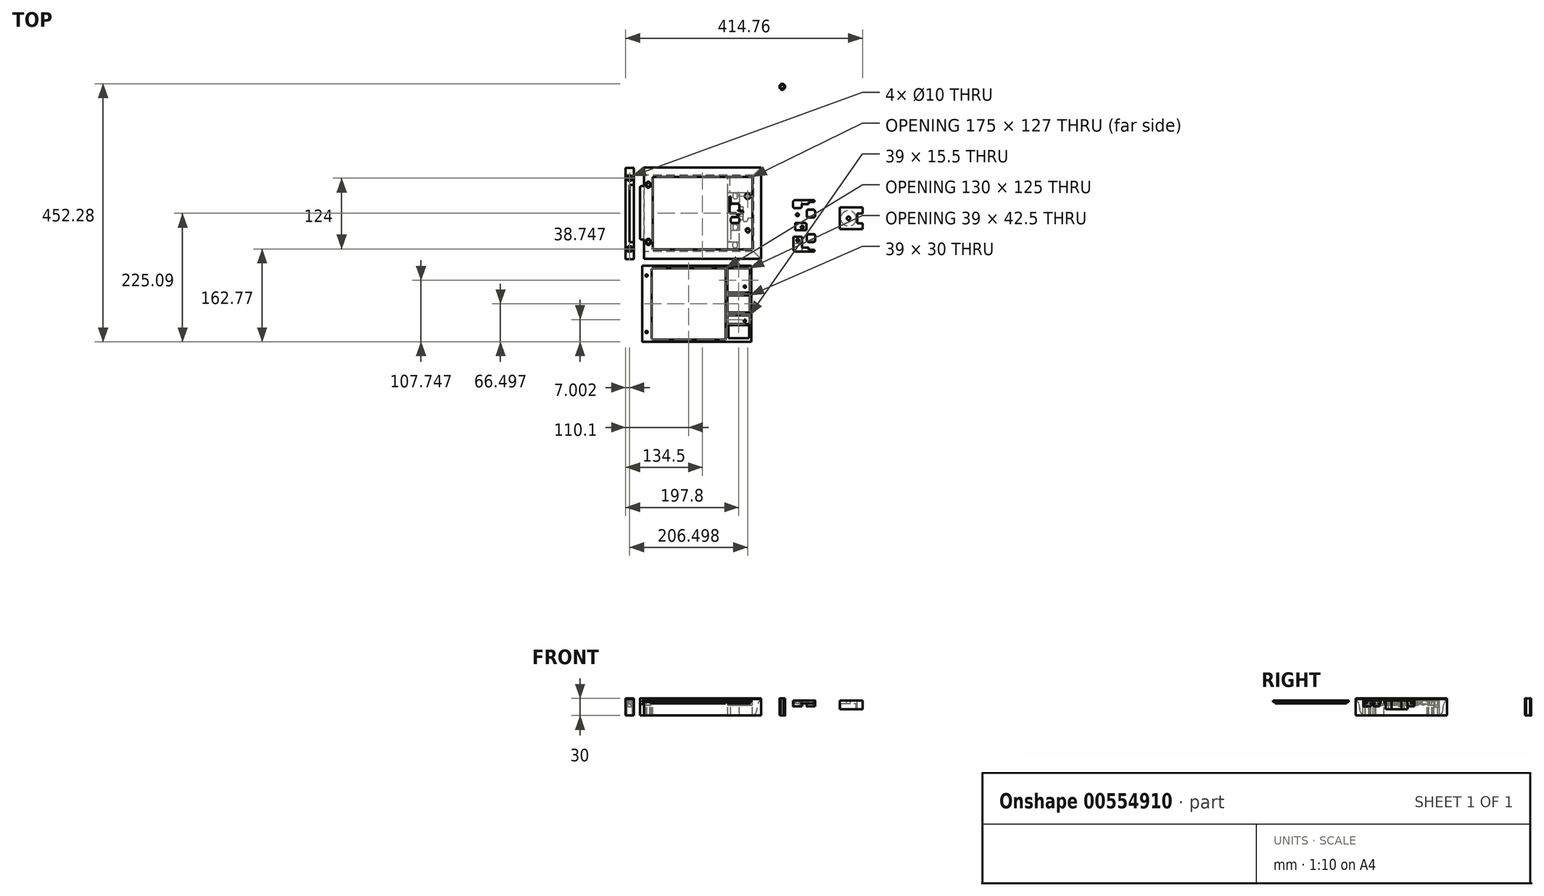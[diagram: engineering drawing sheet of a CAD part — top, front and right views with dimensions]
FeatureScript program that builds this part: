
annotation { "Feature Type Name" : "Feature", "Feature Type Description" : "" }
export const myFeature = defineFeature(function(context is Context, id is Id, definition is map)
    precondition{}
    {
        {
            var Q0;
            Q0=qCreatedBy(makeId("Top.planeOp"),FACE);
            var sketch = newSketch(context, id + "F0", { "sketchPlane" : qUnion([Q0])});
            skLineSegment(sketch, "E0.bottom", {"start": v(-107.5, 80) * mm, "end": v(97.5, 80) * mm});
            skLineSegment(sketch, "E0.top", {"start": v(-97.5, 0) * mm, "end": v(97.5, 0) * mm, "construction": true});
            skLineSegment(sketch, "E0.right", {"start": v(97.5, 80) * mm, "end": v(97.5, 0) * mm});
            skLineSegment(sketch, "E1.bottom", {"start": v(-92.5, 63.5) * mm, "end": v(82.5, 63.5) * mm});
            skLineSegment(sketch, "E1.left", {"start": v(-107.5, 63.5) * mm, "end": v(-107.5, -5) * mm});
            skLineSegment(sketch, "E1.right", {"start": v(82.5, 63.5) * mm, "end": v(82.5, 0) * mm});
            skLineSegment(sketch, "E2.right", {"start": v(42.5, 65) * mm, "end": v(42.5, 0) * mm});
            skLineSegment(sketch, "E3.MirrorCS", {"start": v(-92.5, -63.5) * mm, "end": v(82.5, -63.5) * mm});
            skLineSegment(sketch, "E4.MirrorCS", {"start": v(-107.5, -63.5) * mm, "end": v(-107.5, 5) * mm});
            skLineSegment(sketch, "E5.MirrorCS", {"start": v(-107.5, -80) * mm, "end": v(97.5, -80) * mm});
            skLineSegment(sketch, "E6.MirrorCS", {"start": v(97.5, -80) * mm, "end": v(97.5, 0) * mm});
            skLineSegment(sketch, "E7.MirrorCS", {"start": v(47.5, -4.97) * mm, "end": v(56.5, -4.97) * mm});
            skLineSegment(sketch, "E8.MirrorCS", {"start": v(44.5, -13.97) * mm, "end": v(44.5, -9.97) * mm});
            skLineSegment(sketch, "E9.MirrorCS", {"start": v(82.5, -63.5) * mm, "end": v(82.5, 0) * mm});
            skLineSegment(sketch, "E10.MirrorCS", {"start": v(59.5, -13.97) * mm, "end": v(59.5, -9.97) * mm});
            skLineSegment(sketch, "E11.MirrorCS", {"start": v(42.5, -63.5) * mm, "end": v(42.5, 0) * mm});
            skLineSegment(sketch, "E12", {"start": v(-107.5, -63.5) * mm, "end": v(-107.5, -80) * mm});
            skLineSegment(sketch, "E13", {"start": v(-107.5, 63.5) * mm, "end": v(-107.5, 80) * mm});
            skLineSegment(sketch, "E14.left", {"start": v(-132.5, 79.68) * mm, "end": v(-132.5, -0.32) * mm});
            skLineSegment(sketch, "E15.MirrorCS", {"start": v(-132.5, -80.32) * mm, "end": v(-132.5, -10.32) * mm});
            skPoint(sketch, "E16", {"position": v(-132.5, -50.32) * mm});
            skLineSegment(sketch, "E17", {"start": v(-132.5, -50.32) * mm, "end": v(-127.5, -50.32) * mm});
            skPoint(sketch, "E18", {"position": v(-132.5, 49.68) * mm});
            skLineSegment(sketch, "E19", {"start": v(-132.5, 49.68) * mm, "end": v(-127.5, 49.68) * mm});
            skLineSegment(sketch, "E20", {"start": v(-114.5, -30.14) * mm, "end": v(-114.5, 44.86) * mm});
            skLineSegment(sketch, "E21", {"start": v(-127.5, -50.32) * mm, "end": v(-125.5, -50.32) * mm});
            skLineSegment(sketch, "E22", {"start": v(-125.5, -50.32) * mm, "end": v(-125.5, -80.32) * mm});
            skLineSegment(sketch, "E23", {"start": v(-125.5, -50.32) * mm, "end": v(-125.5, 79.68) * mm});
            skLineSegment(sketch, "E24", {"start": v(-127.5, 49.68) * mm, "end": v(-125.5, 49.68) * mm});
            skLineSegment(sketch, "E25", {"start": v(-107.5, -80) * mm, "end": v(-92.5, -80) * mm});
            skLineSegment(sketch, "E26", {"start": v(-92.5, -80) * mm, "end": v(-92.5, 63.5) * mm});
            skLineSegment(sketch, "E27", {"start": v(47.5, -16.97) * mm, "end": v(56.5, -16.97) * mm});
            skLineSegment(sketch, "E28", {"start": v(47.5, -6.97) * mm, "end": v(56.5, -6.97) * mm});
            skLineSegment(sketch, "E29", {"start": v(47.5, -18.97) * mm, "end": v(56.5, -18.97) * mm});
            skLineSegment(sketch, "E30", {"start": v(46.02, -30.47) * mm, "end": v(53.02, -30.47) * mm});
            skLineSegment(sketch, "E31", {"start": v(44.5, -63.15) * mm, "end": v(56.5, -63.15) * mm});
            skLineSegment(sketch, "E32", {"start": v(59.5, -58.47) * mm, "end": v(59.5, -51.47) * mm});
            skArc(sketch, "E33.filletArc", {"start": v(47.5, -4.97) * mm, "mid": v(45.38, -5.85) * mm, "end": v(44.5, -7.97) * mm});
            skLineSegment(sketch, "E34", {"start": v(44.5, -45) * mm, "end": v(44.5, -27.47) * mm});
            skLineSegment(sketch, "E35", {"start": v(59.5, -27.47) * mm, "end": v(59.5, -45) * mm});
            skCircle(sketch, "E36", {"center": v(52, -55.5) * mm, "radius": 2.55 * mm});
            skCircle(sketch, "E37.MirrorC", {"center": v(52, 30.47) * mm, "radius": 2.55 * mm});
            skLineSegment(sketch, "E38.MirrorCS", {"start": v(44.5, 36.5) * mm, "end": v(44.5, 27.47) * mm});
            skLineSegment(sketch, "E39.MirrorCS", {"start": v(59.5, 27.47) * mm, "end": v(59.5, 33.5) * mm});
            skLineSegment(sketch, "E40", {"start": v(44.5, -49.9) * mm, "end": v(57.5, -49.9) * mm});
            skLineSegment(sketch, "E41", {"start": v(-132.5, 79.68) * mm, "end": v(-125.5, 79.68) * mm});
            skLineSegment(sketch, "E42", {"start": v(-132.5, -80.32) * mm, "end": v(-125.5, -80.32) * mm});
            skLineSegment(sketch, "E43", {"start": v(39.5, 36.5) * mm, "end": v(44.5, 36.5) * mm});
            skLineSegment(sketch, "E44", {"start": v(39.5, 29.5) * mm, "end": v(44.5, 29.5) * mm});
            skLineSegment(sketch, "E45", {"start": v(82.5, 0) * mm, "end": v(42.5, 0) * mm});
            skCircle(sketch, "E46", {"center": v(57.5, 0) * mm, "radius": 3 * mm});
            skLineSegment(sketch, "E47", {"start": v(47.9, 28.33) * mm, "end": v(47.9, 32.6) * mm});
            skLineSegment(sketch, "E48", {"start": v(56.1, 28.33) * mm, "end": v(56.1, 32.6) * mm});
            skLineSegment(sketch, "E49", {"start": v(50.28, 25.92) * mm, "end": v(47.9, 27.58) * mm});
            skLineSegment(sketch, "E50", {"start": v(53.72, 25.92) * mm, "end": v(56.1, 27.58) * mm});
            skLineSegment(sketch, "E51", {"start": v(53.72, 35.02) * mm, "end": v(56.1, 33.36) * mm});
            skLineSegment(sketch, "E52", {"start": v(50.28, 35.02) * mm, "end": v(47.9, 33.36) * mm});
            skLineSegment(sketch, "E53", {"start": v(47.9, -57.64) * mm, "end": v(47.9, -53.37) * mm});
            skLineSegment(sketch, "E54", {"start": v(56.1, -57.64) * mm, "end": v(56.1, -53.37) * mm});
            skLineSegment(sketch, "E55", {"start": v(50.28, -60.05) * mm, "end": v(47.9, -58.4) * mm});
            skLineSegment(sketch, "E56", {"start": v(53.72, -60.05) * mm, "end": v(56.1, -58.4) * mm});
            skLineSegment(sketch, "E57", {"start": v(53.72, -50.94) * mm, "end": v(56.1, -52.6) * mm});
            skLineSegment(sketch, "E58", {"start": v(50.28, -50.94) * mm, "end": v(47.9, -52.6) * mm});
            skCircle(sketch, "E59.MirrorC", {"center": v(52, -24.47) * mm, "radius": 2.55 * mm});
            skLineSegment(sketch, "E60", {"start": v(47.9, -26.61) * mm, "end": v(47.9, -22.33) * mm});
            skLineSegment(sketch, "E61", {"start": v(56.1, -26.61) * mm, "end": v(56.1, -22.33) * mm});
            skLineSegment(sketch, "E62", {"start": v(50.28, -29.02) * mm, "end": v(47.9, -27.36) * mm});
            skLineSegment(sketch, "E63", {"start": v(53.72, -29.02) * mm, "end": v(56.1, -27.36) * mm});
            skLineSegment(sketch, "E64", {"start": v(53.72, -19.92) * mm, "end": v(56.1, -21.58) * mm});
            skLineSegment(sketch, "E65", {"start": v(50.28, -19.92) * mm, "end": v(47.9, -21.58) * mm});
            skArc(sketch, "E66.filletArc", {"start": v(44.5, -13.97) * mm, "mid": v(45.38, -16.1) * mm, "end": v(47.5, -16.97) * mm});
            skArc(sketch, "E67.filletArc", {"start": v(56.5, -16.97) * mm, "mid": v(58.62, -16.1) * mm, "end": v(59.5, -13.97) * mm});
            skLineSegment(sketch, "E68", {"start": v(44.5, -13.97) * mm, "end": v(44.5, -15.97) * mm});
            skLineSegment(sketch, "E69", {"start": v(59.5, -13.97) * mm, "end": v(59.5, -15.97) * mm});
            skArc(sketch, "E70.filletArc", {"start": v(44.5, -15.97) * mm, "mid": v(45.38, -18.1) * mm, "end": v(47.5, -18.97) * mm});
            skArc(sketch, "E71.filletArc", {"start": v(56.5, -18.97) * mm, "mid": v(58.62, -18.1) * mm, "end": v(59.5, -15.97) * mm});
            skLineSegment(sketch, "E72", {"start": v(44.5, -15.97) * mm, "end": v(44.5, -25.97) * mm});
            skLineSegment(sketch, "E73", {"start": v(59.5, -25.97) * mm, "end": v(59.5, -15.97) * mm});
            skArc(sketch, "E74.filletArc", {"start": v(47.5, -6.97) * mm, "mid": v(45.38, -7.85) * mm, "end": v(44.5, -9.97) * mm});
            skArc(sketch, "E75.filletArc", {"start": v(59.5, -9.97) * mm, "mid": v(58.62, -7.85) * mm, "end": v(56.5, -6.97) * mm});
            skLineSegment(sketch, "E76", {"start": v(44.5, -9.97) * mm, "end": v(44.5, -7.97) * mm});
            skLineSegment(sketch, "E77", {"start": v(44.5, 13.97) * mm, "end": v(44.5, 13.97) * mm});
            skLineSegment(sketch, "E78", {"start": v(59.5, 27.47) * mm, "end": v(59.5, 15.97) * mm});
            skLineSegment(sketch, "E79", {"start": v(59.5, -45) * mm, "end": v(59.5, -51.47) * mm});
            skLineSegment(sketch, "E80", {"start": v(59.5, -58.47) * mm, "end": v(59.5, -60.15) * mm});
            skArc(sketch, "E81.filletArc", {"start": v(56.5, -63.15) * mm, "mid": v(58.62, -62.27) * mm, "end": v(59.5, -60.15) * mm});
            skLineSegment(sketch, "E82", {"start": v(-132.5, -10.32) * mm, "end": v(-132.5, -0.32) * mm});
            skLineSegment(sketch, "E83", {"start": v(-132.5, -50.32) * mm, "end": v(-139.5, -50.32) * mm});
            skLineSegment(sketch, "E84", {"start": v(-132.5, 49.68) * mm, "end": v(-139.5, 49.68) * mm});
            skLineSegment(sketch, "E85", {"start": v(39.5, -63.5) * mm, "end": v(39.5, 63.5) * mm});
            skLineSegment(sketch, "E86", {"start": v(46.02, -30.47) * mm, "end": v(44.5, -30.47) * mm});
            skLineSegment(sketch, "E87", {"start": v(53.02, -30.47) * mm, "end": v(59.5, -30.47) * mm});
            skLineSegment(sketch, "E88", {"start": v(42.5, 29.5) * mm, "end": v(39.5, 29.5) * mm});
            skLineSegment(sketch, "E89", {"start": v(42.5, 36.5) * mm, "end": v(39.5, 36.5) * mm});
            skLineSegment(sketch, "E90", {"start": v(43.5, -49.9) * mm, "end": v(40.5, -49.9) * mm});
            skLineSegment(sketch, "E91", {"start": v(55.5, -49.9) * mm, "end": v(45.5, -49.9) * mm});
            skLineSegment(sketch, "E92", {"start": v(44.5, -30.47) * mm, "end": v(59.5, -30.47) * mm});
            skLineSegment(sketch, "E93", {"start": v(59.5, -30.47) * mm, "end": v(59.5, -50) * mm});
            skLineSegment(sketch, "E94", {"start": v(-111.5, 47.86) * mm, "end": v(-107.5, 47.86) * mm});
            skLineSegment(sketch, "E95", {"start": v(-114.5, -30.14) * mm, "end": v(-114.5, -43.14) * mm});
            skLineSegment(sketch, "E96", {"start": v(-111.5, -46.14) * mm, "end": v(-107.5, -46.14) * mm});
            skPoint(sketch, "E97.end.orphan", {"position": v(-107.5, 59.86) * mm});
            skLineSegment(sketch, "E98", {"start": v(40.5, -49.9) * mm, "end": v(39.5, -49.9) * mm});
            skPoint(sketch, "E99", {"position": v(-100, -50) * mm});
            skLineSegment(sketch, "E100", {"start": v(-103.5, -52.14) * mm, "end": v(-103.5, -47.87) * mm});
            skLineSegment(sketch, "E101", {"start": v(-96.5, -52.14) * mm, "end": v(-96.5, -47.87) * mm});
            skLineSegment(sketch, "E102", {"start": v(-101.72, -54.89) * mm, "end": v(-103.5, -53.64) * mm});
            skLineSegment(sketch, "E103", {"start": v(-98.28, -45.12) * mm, "end": v(-96.5, -46.37) * mm});
            skLineSegment(sketch, "E104", {"start": v(-101.72, -45.12) * mm, "end": v(-103.5, -46.37) * mm});
            skLineSegment(sketch, "E105", {"start": v(-96.5, -53.64) * mm, "end": v(-98.28, -54.89) * mm});
            skLineSegment(sketch, "E106", {"start": v(44.5, -45) * mm, "end": v(44.5, -63.5) * mm});
            skLineSegment(sketch, "E107", {"start": v(59.5, -25.97) * mm, "end": v(59.5, -27.47) * mm});
            skLineSegment(sketch, "E108", {"start": v(44.5, -25.97) * mm, "end": v(44.5, -27.47) * mm});
            skArc(sketch, "E109.filletArc", {"start": v(-114.5, -43.14) * mm, "mid": v(-113.62, -45.26) * mm, "end": v(-111.5, -46.14) * mm});
            skArc(sketch, "E110.filletArc", {"start": v(-111.5, 47.86) * mm, "mid": v(-113.62, 46.98) * mm, "end": v(-114.5, 44.86) * mm});
            skLineSegment(sketch, "E111.MirrorCS", {"start": v(-103.5, 52.14) * mm, "end": v(-103.5, 47.87) * mm});
            skLineSegment(sketch, "E112.MirrorCS", {"start": v(-101.72, 45.12) * mm, "end": v(-103.5, 46.37) * mm});
            skLineSegment(sketch, "E113.MirrorCS", {"start": v(-96.5, 52.14) * mm, "end": v(-96.5, 47.87) * mm});
            skPoint(sketch, "E114.MirrorP", {"position": v(-100, 50) * mm});
            skLineSegment(sketch, "E115.MirrorCS", {"start": v(-96.5, 53.64) * mm, "end": v(-98.28, 54.89) * mm});
            skLineSegment(sketch, "E116.MirrorCS", {"start": v(-98.28, 45.12) * mm, "end": v(-96.5, 46.37) * mm});
            skLineSegment(sketch, "E117.MirrorCS", {"start": v(-101.72, 54.89) * mm, "end": v(-103.5, 53.64) * mm});
            skLineSegment(sketch, "E118", {"start": v(57.5, -63.15) * mm, "end": v(42.5, -63.15) * mm});
            skLineSegment(sketch, "E119", {"start": v(42.5, -63.15) * mm, "end": v(39.5, -63.15) * mm});
            skArc(sketch, "E120.filletArc", {"start": v(53.72, -50.94) * mm, "mid": v(52, -50.4) * mm, "end": v(50.28, -50.94) * mm});
            skArc(sketch, "E121.filletArc", {"start": v(50.28, -60.05) * mm, "mid": v(52, -60.6) * mm, "end": v(53.72, -60.05) * mm});
            skLineSegment(sketch, "E122", {"start": v(47.9, -52.6) * mm, "end": v(47.9, -53.37) * mm});
            skLineSegment(sketch, "E123", {"start": v(56.1, -52.6) * mm, "end": v(56.1, -53.37) * mm});
            skLineSegment(sketch, "E124", {"start": v(47.9, -58.4) * mm, "end": v(47.9, -57.64) * mm});
            skLineSegment(sketch, "E125", {"start": v(56.1, -58.4) * mm, "end": v(56.1, -57.64) * mm});
            skArc(sketch, "E126.filletArc", {"start": v(53.72, -19.92) * mm, "mid": v(52, -19.38) * mm, "end": v(50.28, -19.92) * mm});
            skArc(sketch, "E127.filletArc", {"start": v(50.28, -29.02) * mm, "mid": v(52, -29.56) * mm, "end": v(53.72, -29.02) * mm});
            skLineSegment(sketch, "E128", {"start": v(47.9, -21.58) * mm, "end": v(47.9, -22.33) * mm});
            skLineSegment(sketch, "E129", {"start": v(56.1, -21.58) * mm, "end": v(56.1, -22.33) * mm});
            skLineSegment(sketch, "E130", {"start": v(47.9, -26.61) * mm, "end": v(47.9, -27.36) * mm});
            skLineSegment(sketch, "E131", {"start": v(56.1, -26.61) * mm, "end": v(56.1, -27.36) * mm});
            skArc(sketch, "E132.filletArc", {"start": v(53.72, 35.02) * mm, "mid": v(52, 35.56) * mm, "end": v(50.28, 35.02) * mm});
            skArc(sketch, "E133.filletArc", {"start": v(50.28, 25.92) * mm, "mid": v(52, 25.38) * mm, "end": v(53.72, 25.92) * mm});
            skLineSegment(sketch, "E134", {"start": v(47.9, 28.33) * mm, "end": v(47.9, 27.58) * mm});
            skLineSegment(sketch, "E135", {"start": v(56.1, 28.33) * mm, "end": v(56.1, 27.58) * mm});
            skLineSegment(sketch, "E136", {"start": v(47.9, 33.36) * mm, "end": v(47.9, 32.6) * mm});
            skLineSegment(sketch, "E137", {"start": v(56.1, 33.36) * mm, "end": v(56.1, 32.6) * mm});
            skArc(sketch, "E138.filletArc", {"start": v(-98.28, 54.89) * mm, "mid": v(-100, 55.43) * mm, "end": v(-101.72, 54.89) * mm});
            skArc(sketch, "E139.filletArc", {"start": v(-101.72, 45.12) * mm, "mid": v(-100, 44.58) * mm, "end": v(-98.28, 45.12) * mm});
            skArc(sketch, "E140.filletArc", {"start": v(-101.72, -54.89) * mm, "mid": v(-100, -55.43) * mm, "end": v(-98.28, -54.89) * mm});
            skArc(sketch, "E141.filletArc", {"start": v(-98.28, -45.12) * mm, "mid": v(-100, -44.58) * mm, "end": v(-101.72, -45.12) * mm});
            skLineSegment(sketch, "E142", {"start": v(57.5, -49.9) * mm, "end": v(59.5, -49.9) * mm});
            skLineSegment(sketch, "E143", {"start": v(39.5, -49.9) * mm, "end": v(44.5, -49.9) * mm});
            skLineSegment(sketch, "E144", {"start": v(-103.5, 46.37) * mm, "end": v(-103.5, 47.87) * mm});
            skLineSegment(sketch, "E145", {"start": v(-103.5, 52.14) * mm, "end": v(-103.5, 53.64) * mm});
            skLineSegment(sketch, "E146", {"start": v(-96.49, 52.16) * mm, "end": v(-96.5, 53.64) * mm});
            skLineSegment(sketch, "E147", {"start": v(-96.5, 46.37) * mm, "end": v(-96.5, 47.87) * mm});
            skLineSegment(sketch, "E148", {"start": v(-103.5, -53.64) * mm, "end": v(-103.5, -52.14) * mm});
            skLineSegment(sketch, "E149", {"start": v(-103.53, -47.9) * mm, "end": v(-103.5, -46.37) * mm});
            skLineSegment(sketch, "E150", {"start": v(-96.5, -47.87) * mm, "end": v(-96.5, -46.37) * mm});
            skLineSegment(sketch, "E151", {"start": v(-96.5, -53.64) * mm, "end": v(-96.5, -52.14) * mm});
            skCircle(sketch, "E152", {"center": v(-132.5, -62.32) * mm, "radius": 3.1 * mm});
            skCircle(sketch, "E153", {"center": v(-132.5, -62.32) * mm, "radius": 5 * mm});
            skLineSegment(sketch, "E154", {"start": v(-132.5, -0.32) * mm, "end": v(-139.5, -0.32) * mm});
            skCircle(sketch, "E155.MirrorC", {"center": v(-132.5, 61.68) * mm, "radius": 5 * mm});
            skCircle(sketch, "E156.MirrorC", {"center": v(-132.5, 61.68) * mm, "radius": 3.1 * mm});
            skLineSegment(sketch, "E157", {"start": v(-132.5, 79.68) * mm, "end": v(-139.5, 79.68) * mm});
            skLineSegment(sketch, "E158", {"start": v(-139.5, 79.68) * mm, "end": v(-139.5, -80.32) * mm});
            skLineSegment(sketch, "E159", {"start": v(-139.5, -80.32) * mm, "end": v(-132.5, -80.32) * mm});
            skCircle(sketch, "E160", {"center": v(-100, -50) * mm, "radius": 3.15 * mm});
            skCircle(sketch, "E161", {"center": v(-100, -50) * mm, "radius": 5 * mm});
            skCircle(sketch, "E162", {"center": v(-100, 50) * mm, "radius": 3.15 * mm});
            skCircle(sketch, "E163", {"center": v(-100, 50) * mm, "radius": 4.74 * mm});
            skLineSegment(sketch, "E164", {"start": v(44.5, 36.5) * mm, "end": v(56.5, 36.5) * mm});
            skArc(sketch, "E165.filletArc", {"start": v(59.5, 33.5) * mm, "mid": v(58.62, 35.62) * mm, "end": v(56.5, 36.5) * mm});
            skLineSegment(sketch, "E166", {"start": v(56.5, 36.5) * mm, "end": v(82.5, 36.5) * mm});
            skLineSegment(sketch, "E167", {"start": v(82.5, -8.5) * mm, "end": v(73.96, -8.5) * mm});
            skLineSegment(sketch, "E168", {"start": v(73.96, 8.5) * mm, "end": v(82.5, 8.5) * mm});
            skLineSegment(sketch, "E169", {"start": v(59.5, 11.47) * mm, "end": v(71.5, 11.48) * mm});
            skLineSegment(sketch, "E170", {"start": v(71.5, 11.48) * mm, "end": v(71.5, 4.98) * mm});
            skLineSegment(sketch, "E171", {"start": v(73.96, 8.5) * mm, "end": v(73.96, 11.5) * mm});
            skLineSegment(sketch, "E172", {"start": v(70.96, 14.5) * mm, "end": v(68.96, 14.5) * mm});
            skLineSegment(sketch, "E173", {"start": v(65.96, 11.5) * mm, "end": v(65.96, 0) * mm});
            skLineSegment(sketch, "E174.MirrorCS", {"start": v(71.5, -11.48) * mm, "end": v(71.5, -4.98) * mm});
            skLineSegment(sketch, "E175.MirrorCS", {"start": v(70.96, -14.5) * mm, "end": v(68.96, -14.5) * mm});
            skLineSegment(sketch, "E176.MirrorCS", {"start": v(73.96, -8.5) * mm, "end": v(73.96, -11.5) * mm});
            skLineSegment(sketch, "E177.MirrorCS", {"start": v(56.5, -4.97) * mm, "end": v(56.5, -4.97) * mm});
            skLineSegment(sketch, "E178.MirrorCS", {"start": v(59.5, -11.47) * mm, "end": v(71.5, -11.48) * mm});
            skLineSegment(sketch, "E179.MirrorCS", {"start": v(65.96, -11.5) * mm, "end": v(65.96, 0) * mm});
            skArc(sketch, "E180.filletArc", {"start": v(73.96, 11.5) * mm, "mid": v(73.08, 13.62) * mm, "end": v(70.96, 14.5) * mm});
            skArc(sketch, "E181.filletArc", {"start": v(68.96, 14.5) * mm, "mid": v(66.84, 13.62) * mm, "end": v(65.96, 11.5) * mm});
            skArc(sketch, "E182.filletArc", {"start": v(70.96, -14.5) * mm, "mid": v(73.08, -13.62) * mm, "end": v(73.96, -11.5) * mm});
            skArc(sketch, "E183.filletArc", {"start": v(65.96, -11.5) * mm, "mid": v(66.84, -13.62) * mm, "end": v(68.96, -14.5) * mm});
            skLineSegment(sketch, "E184", {"start": v(59.5, -9.97) * mm, "end": v(59.5, -7.97) * mm});
            skPoint(sketch, "E185.newPointA", {"position": v(71.5, 4.98) * mm});
            skLineSegment(sketch, "E186", {"start": v(56.5, 4.97) * mm, "end": v(71.5, 4.98) * mm});
            skPoint(sketch, "E187.newPointB", {"position": v(71.5, -4.98) * mm});
            skArc(sketch, "E187.filletArc", {"start": v(59.5, -7.97) * mm, "mid": v(58.62, -5.85) * mm, "end": v(56.5, -4.97) * mm});
            skLineSegment(sketch, "E188", {"start": v(56.5, -4.97) * mm, "end": v(71.5, -4.98) * mm});
            skLineSegment(sketch, "E189", {"start": v(44.5, 15.97) * mm, "end": v(44.5, 27.47) * mm});
            skLineSegment(sketch, "E190.MirrorCS", {"start": v(56.5, 4.97) * mm, "end": v(56.5, 4.97) * mm});
            skLineSegment(sketch, "E191.MirrorCS", {"start": v(59.5, 13.97) * mm, "end": v(59.5, 15.97) * mm});
            skLineSegment(sketch, "E192.MirrorCS", {"start": v(44.5, 9.97) * mm, "end": v(44.5, 7.97) * mm});
            skLineSegment(sketch, "E193.MirrorCS", {"start": v(47.5, 18.97) * mm, "end": v(56.5, 18.97) * mm});
            skLineSegment(sketch, "E194.MirrorCS", {"start": v(47.5, 6.97) * mm, "end": v(56.5, 6.97) * mm});
            skLineSegment(sketch, "E195.MirrorCS", {"start": v(47.5, 4.97) * mm, "end": v(56.5, 4.97) * mm});
            skArc(sketch, "E196.MirrorCS", {"start": v(47.5, 6.97) * mm, "mid": v(45.38, 7.85) * mm, "end": v(44.5, 9.97) * mm});
            skArc(sketch, "E197.MirrorCS", {"start": v(56.5, 16.97) * mm, "mid": v(58.62, 16.1) * mm, "end": v(59.5, 13.97) * mm});
            skLineSegment(sketch, "E198.MirrorCS", {"start": v(44.5, 13.97) * mm, "end": v(44.5, 15.97) * mm});
            skLineSegment(sketch, "E199.MirrorCS", {"start": v(59.5, 9.97) * mm, "end": v(59.5, 7.97) * mm});
            skArc(sketch, "E200.MirrorCS", {"start": v(47.5, 4.97) * mm, "mid": v(45.38, 5.85) * mm, "end": v(44.5, 7.97) * mm});
            skArc(sketch, "E201.MirrorCS", {"start": v(44.5, 13.97) * mm, "mid": v(45.38, 16.1) * mm, "end": v(47.5, 16.97) * mm});
            skArc(sketch, "E202.MirrorCS", {"start": v(44.5, 15.97) * mm, "mid": v(45.38, 18.1) * mm, "end": v(47.5, 18.97) * mm});
            skLineSegment(sketch, "E203.MirrorCS", {"start": v(44.5, 13.97) * mm, "end": v(44.5, 9.97) * mm});
            skLineSegment(sketch, "E204.MirrorCS", {"start": v(47.5, 16.97) * mm, "end": v(56.5, 16.97) * mm});
            skLineSegment(sketch, "E205.MirrorCS", {"start": v(59.5, 13.97) * mm, "end": v(59.5, 9.97) * mm});
            skArc(sketch, "E206.MirrorCS", {"start": v(59.5, 7.97) * mm, "mid": v(58.62, 5.85) * mm, "end": v(56.5, 4.97) * mm});
            skArc(sketch, "E207.MirrorCS", {"start": v(56.5, 18.97) * mm, "mid": v(58.62, 18.1) * mm, "end": v(59.5, 15.97) * mm});
            skArc(sketch, "E208.MirrorCS", {"start": v(59.5, 9.97) * mm, "mid": v(58.62, 7.85) * mm, "end": v(56.5, 6.97) * mm});
            skLineSegment(sketch, "E209.MirrorCS", {"start": v(131.25, 223.9) * mm, "end": v(131.25, 225.4) * mm});
            skLineSegment(sketch, "E210.MirrorCS", {"start": v(138.25, 223.9) * mm, "end": v(138.25, 219.63) * mm});
            skLineSegment(sketch, "E211.MirrorCS", {"start": v(138.25, 225.4) * mm, "end": v(136.47, 226.65) * mm});
            skLineSegment(sketch, "E212.MirrorCS", {"start": v(131.25, 219.63) * mm, "end": v(131.25, 218.13) * mm});
            skArc(sketch, "E213.MirrorCS", {"start": v(133.03, 226.65) * mm, "mid": v(134.75, 227.19) * mm, "end": v(136.47, 226.65) * mm});
            skLineSegment(sketch, "E214.MirrorCS", {"start": v(138.25, 219.63) * mm, "end": v(138.25, 218.13) * mm});
            skLineSegment(sketch, "E215.MirrorCS", {"start": v(131.25, 223.9) * mm, "end": v(131.25, 219.63) * mm});
            skLineSegment(sketch, "E216.MirrorCS", {"start": v(133.03, 226.65) * mm, "end": v(131.25, 225.4) * mm});
            skLineSegment(sketch, "E217.MirrorCS", {"start": v(136.47, 216.88) * mm, "end": v(138.25, 218.13) * mm});
            skLineSegment(sketch, "E218.MirrorCS", {"start": v(133.03, 216.88) * mm, "end": v(131.25, 218.13) * mm});
            skArc(sketch, "E219.MirrorCS", {"start": v(136.47, 216.88) * mm, "mid": v(134.75, 216.34) * mm, "end": v(133.03, 216.88) * mm});
            skPoint(sketch, "E220.MirrorP", {"position": v(134.75, 221.76) * mm});
            skLineSegment(sketch, "E221.MirrorCS", {"start": v(138.25, 223.9) * mm, "end": v(138.25, 225.4) * mm});
            skCircle(sketch, "E222", {"center": v(134.75, 221.76) * mm, "radius": 5 * mm});
            skCircle(sketch, "E223", {"center": v(134.75, 221.76) * mm, "radius": 3.15 * mm});
            skCircle(sketch, "E224", {"center": v(74, -30) * mm, "radius": 3.15 * mm});
            skCircle(sketch, "E225", {"center": v(74, -30) * mm, "radius": 5 * mm});
            skCircle(sketch, "E226.MirrorC", {"center": v(74, 30) * mm, "radius": 5 * mm});
            skCircle(sketch, "E227.MirrorC", {"center": v(74, 30) * mm, "radius": 3.15 * mm});
            skSolve(sketch);
        }
        {
            var Q0;
            {var subQ6=sQuery(id+"F0.wireOp",EDGE,"RdLYVHK0-ZMMy-n2T9-vo5N-ViF6aoFnglOa");Q0=makeQuery(id+"F0.imprint","IMPRINT",FACE,{"disambiguationData":[TD([[makeQuery(id+"F0.imprint","IMPRINT",EDGE,{"derivedFrom":subQ6}),-1.0]])]});}
            var Q1;
            {var subQ6=sQuery(id+"F0.wireOp",EDGE,"E40");Q1=makeQuery(id+"F0.imprint","IMPRINT",FACE,{"disambiguationData":[TD([[makeQuery(id+"F0.imprint","IMPRINT",EDGE,{"derivedFrom":subQ6}),-1.0]])]});}
            var Q2;
            {var subQ8=sQuery(id+"F0.wireOp",EDGE,"E39.MirrorCS");Q2=makeQuery(id+"F0.imprint","IMPRINT",FACE,{"disambiguationData":[TD([[makeQuery(id+"F0.imprint","IMPRINT",EDGE,{"derivedFrom":subQ8}),1.0]])]});}
            var Q3;
            Q3=makeQuery(id+"F0.imprint","IMPRINT",FACE,{"disambiguationData":[TD([[makeQuery(id+"F0.imprint","IMPRINT",EDGE,{"derivedFrom":sQuery(id+"F0.wireOp",EDGE,"E30")}),-1.0]])]});
            var Q4;
            {var subQ8=sQuery(id+"F0.wireOp",EDGE,"12c242b3-208e-4177-b4b7-cfe86d31bad3.filletArc");Q4=makeQuery(id+"F0.imprint","IMPRINT",FACE,{"disambiguationData":[TD([[makeQuery(id+"F0.imprint","IMPRINT",EDGE,{"derivedFrom":subQ8}),1.0]])]});}
            var Q5;
            {var subQ5=sQuery(id+"F0.wireOp",EDGE,"E31");Q5=makeQuery(id+"F0.imprint","IMPRINT",FACE,{"disambiguationData":[TD([[makeQuery(id+"F0.imprint","IMPRINT",EDGE,{"derivedFrom":subQ5}),1.0]])]});}
            var Q6;
            Q6=makeQuery(id+"F0.imprint","IMPRINT",FACE,{"disambiguationData":[TD([[makeQuery(id+"F0.imprint","IMPRINT",EDGE,{"derivedFrom":sQuery(id+"F0.wireOp",EDGE,"E7.MirrorCS")}),-1.0]])]});
            var Q7;
            {var subQ5=sQuery(id+"F0.wireOp",EDGE,"6d39de08-ad94-4231-b662-17a660603f591.MirrorCS");Q7=makeQuery(id+"F0.imprint","IMPRINT",FACE,{"disambiguationData":[TD([[makeQuery(id+"F0.imprint","IMPRINT",EDGE,{"derivedFrom":subQ5}),-1.0]])]});}
            var Q8;
            Q8=makeQuery(id+"F0.imprint","IMPRINT",FACE,{"disambiguationData":[TD([[makeQuery(id+"F0.imprint","IMPRINT",EDGE,{"derivedFrom":sQuery(id+"F0.wireOp",EDGE,"E47")}),-1.0]])]});
            var Q9;
            {var subQ4=sQuery(id+"F0.wireOp",EDGE,"E53");Q9=makeQuery(id+"F0.imprint","IMPRINT",FACE,{"disambiguationData":[TD([[makeQuery(id+"F0.imprint","IMPRINT",EDGE,{"derivedFrom":subQ4}),-1.0]])]});}
            var Q10;
            {var subQ0=sQuery(id+"F0.wireOp",EDGE,"6d39de08-ad94-4231-b662-17a660603f594.MirrorC");var subQ1=sQuery(id+"F0.wireOp",EDGE,"E37.MirrorC");var subQ2=makeQuery(id+"F0.imprint","INTERSECT",VERTEX,{"disambiguationData":[OD(0.0)],"derivedFrom":[subQ1,subQ0]});Q10=makeQuery(id+"F0.imprint","IMPRINT",FACE,{"disambiguationData":[TD([[makeQuery(id+"F0.imprint","IMPRINT",EDGE,{"disambiguationData":[TD([[subQ2,-1.0]])],"derivedFrom":subQ1}),-1.0]])]});}
            var Q11;
            {var subQ5=sQuery(id+"F0.wireOp",EDGE,"2Ry4WlIC-CQQb-5CF8-FWkS-usfLcIxYfUWP");Q11=makeQuery(id+"F0.imprint","IMPRINT",FACE,{"disambiguationData":[TD([[makeQuery(id+"F0.imprint","IMPRINT",EDGE,{"derivedFrom":subQ5}),-1.0]])]});}
            var Q12;
            Q12=makeQuery(id+"F0.imprint","IMPRINT",FACE,{"disambiguationData":[TD([[makeQuery(id+"F0.imprint","IMPRINT",EDGE,{"derivedFrom":sQuery(id+"F0.wireOp",EDGE,"E59.MirrorC")}),1.0]])]});
            var Q13;
            Q13=makeQuery(id+"F0.imprint","IMPRINT",FACE,{"disambiguationData":[TD([[makeQuery(id+"F0.imprint","IMPRINT",EDGE,{"derivedFrom":sQuery(id+"F0.wireOp",EDGE,"E59.MirrorC")}),-1.0]])]});
            var Q14;
            {var subQ0=sQuery(id+"F0.wireOp",EDGE,"da70cb73-bd24-4d72-8de4-aa27c8984207.MirrorC");var subQ1=sQuery(id+"F0.wireOp",EDGE,"E36");var subQ2=makeQuery(id+"F0.imprint","INTERSECT",VERTEX,{"disambiguationData":[OD(0.0)],"derivedFrom":[subQ1,subQ0]});Q14=makeQuery(id+"F0.imprint","IMPRINT",FACE,{"disambiguationData":[TD([[makeQuery(id+"F0.imprint","IMPRINT",EDGE,{"disambiguationData":[TD([[subQ2,-1.0]])],"derivedFrom":subQ1}),1.0]])]});}
            var Q15;
            {var subQ0=sQuery(id+"F0.wireOp",EDGE,"da70cb73-bd24-4d72-8de4-aa27c8984207.MirrorC");var subQ1=sQuery(id+"F0.wireOp",EDGE,"E36");var subQ2=makeQuery(id+"F0.imprint","INTERSECT",VERTEX,{"disambiguationData":[OD(0.0)],"derivedFrom":[subQ1,subQ0]});Q15=makeQuery(id+"F0.imprint","IMPRINT",FACE,{"disambiguationData":[TD([[makeQuery(id+"F0.imprint","IMPRINT",EDGE,{"disambiguationData":[TD([[subQ2,1.0]])],"derivedFrom":subQ1}),1.0]])]});}
            var Q16;
            Q16=makeQuery(id+"F0.imprint","IMPRINT",FACE,{"disambiguationData":[TD([[makeQuery(id+"F0.imprint","IMPRINT",EDGE,{"derivedFrom":sQuery(id+"F0.wireOp",EDGE,"E27")}),-1.0]])]});
            var Q17;
            Q17=makeQuery(id+"F0.imprint","IMPRINT",FACE,{"disambiguationData":[TD([[makeQuery(id+"F0.imprint","IMPRINT",EDGE,{"derivedFrom":sQuery(id+"F0.wireOp",EDGE,"E30")}),1.0]])]});
            var Q18;
            {var subQ0=sQuery(id+"F0.wireOp",EDGE,"6d39de08-ad94-4231-b662-17a660603f594.MirrorC");var subQ1=sQuery(id+"F0.wireOp",EDGE,"E37.MirrorC");var subQ2=makeQuery(id+"F0.imprint","INTERSECT",VERTEX,{"disambiguationData":[OD(1.0)],"derivedFrom":[subQ1,subQ0]});Q18=makeQuery(id+"F0.imprint","IMPRINT",FACE,{"disambiguationData":[TD([[makeQuery(id+"F0.imprint","IMPRINT",EDGE,{"disambiguationData":[TD([[subQ2,1.0]])],"derivedFrom":subQ1}),-1.0]])]});}
            var Q19;
            {var subQ0=sQuery(id+"F0.wireOp",EDGE,"6d39de08-ad94-4231-b662-17a660603f594.MirrorC");var subQ1=sQuery(id+"F0.wireOp",EDGE,"E37.MirrorC");var subQ2=makeQuery(id+"F0.imprint","INTERSECT",VERTEX,{"disambiguationData":[OD(0.0)],"derivedFrom":[subQ1,subQ0]});Q19=makeQuery(id+"F0.imprint","IMPRINT",FACE,{"disambiguationData":[TD([[makeQuery(id+"F0.imprint","IMPRINT",EDGE,{"disambiguationData":[TD([[subQ2,-1.0]])],"derivedFrom":subQ1}),1.0]])]});}
            var Q20;
            {var subQ0=sQuery(id+"F0.wireOp",EDGE,"da70cb73-bd24-4d72-8de4-aa27c8984207.MirrorC");var subQ1=sQuery(id+"F0.wireOp",EDGE,"E36");var subQ2=makeQuery(id+"F0.imprint","INTERSECT",VERTEX,{"disambiguationData":[OD(0.0)],"derivedFrom":[subQ1,subQ0]});Q20=makeQuery(id+"F0.imprint","IMPRINT",FACE,{"disambiguationData":[TD([[makeQuery(id+"F0.imprint","IMPRINT",EDGE,{"disambiguationData":[TD([[subQ2,-1.0]])],"derivedFrom":subQ1}),-1.0]])]});}
            var Q21;
            {var subQ0=sQuery(id+"F0.wireOp",EDGE,"E56");var subQ1=sQuery(id+"F0.wireOp",EDGE,"JaYlbfzk-Zl2f-mc1O-yia5-9wafT0kwsFXx");var subQ2=makeQuery(id+"F0.imprint","INTERSECT",VERTEX,{"derivedFrom":[subQ1,subQ0]});Q21=makeQuery(id+"F0.imprint","IMPRINT",FACE,{"disambiguationData":[TD([[makeQuery(id+"F0.imprint","IMPRINT",EDGE,{"disambiguationData":[TD([[subQ2,-1.0]])],"derivedFrom":subQ1}),1.0]])]});}
            var Q22;
            {var subQ0=sQuery(id+"F0.wireOp",EDGE,"E65");var subQ1=sQuery(id+"F0.wireOp",EDGE,"E29");var subQ2=makeQuery(id+"F0.imprint","INTERSECT",VERTEX,{"derivedFrom":[subQ1,subQ0]});Q22=makeQuery(id+"F0.imprint","IMPRINT",FACE,{"disambiguationData":[TD([[makeQuery(id+"F0.imprint","IMPRINT",EDGE,{"disambiguationData":[TD([[subQ2,-1.0]])],"derivedFrom":subQ1}),1.0]])]});}
            var Q23;
            {var subQ3=sQuery(id+"F0.wireOp",EDGE,"539c7ef6-e73b-46dd-b7a3-ca27ce5554f6.filletArc");Q23=makeQuery(id+"F0.imprint","IMPRINT",FACE,{"disambiguationData":[TD([[makeQuery(id+"F0.imprint","IMPRINT",EDGE,{"derivedFrom":subQ3}),-1.0]])]});}
            var Q24;
            {var subQ3=sQuery(id+"F0.wireOp",EDGE,"12c242b3-208e-4177-b4b7-cfe86d31bad3.filletArc");Q24=makeQuery(id+"F0.imprint","IMPRINT",FACE,{"disambiguationData":[TD([[makeQuery(id+"F0.imprint","IMPRINT",EDGE,{"derivedFrom":subQ3}),-1.0]])]});}
            var Q25;
            {var subQ3=sQuery(id+"F0.wireOp",EDGE,"0847fe41-721d-4950-b82d-f0747cbaa81d.filletArc");Q25=makeQuery(id+"F0.imprint","IMPRINT",FACE,{"disambiguationData":[TD([[makeQuery(id+"F0.imprint","IMPRINT",EDGE,{"derivedFrom":subQ3}),-1.0]])]});}
            var Q26;
            {var subQ3=sQuery(id+"F0.wireOp",EDGE,"e0f77c02-860a-4edd-adaa-7ff4540aa646.filletArc");Q26=makeQuery(id+"F0.imprint","IMPRINT",FACE,{"disambiguationData":[TD([[makeQuery(id+"F0.imprint","IMPRINT",EDGE,{"derivedFrom":subQ3}),-1.0]])]});}
            var Q27;
            {var subQ3=sQuery(id+"F0.wireOp",EDGE,"3c7ebc2a-9bb0-4856-9a0a-d8b2cbd53c78.filletArc");Q27=makeQuery(id+"F0.imprint","IMPRINT",FACE,{"disambiguationData":[TD([[makeQuery(id+"F0.imprint","IMPRINT",EDGE,{"derivedFrom":subQ3}),-1.0]])]});}
            var Q28;
            {var subQ3=sQuery(id+"F0.wireOp",EDGE,"97454885-adff-4b19-a790-fbf4b010259c.filletArc");Q28=makeQuery(id+"F0.imprint","IMPRINT",FACE,{"disambiguationData":[TD([[makeQuery(id+"F0.imprint","IMPRINT",EDGE,{"derivedFrom":subQ3}),-1.0]])]});}
            var Q29;
            Q29=makeQuery(id+"F0.imprint","IMPRINT",FACE,{"disambiguationData":[TD([[makeQuery(id+"F0.imprint","IMPRINT",EDGE,{"derivedFrom":sQuery(id+"F0.wireOp",EDGE,"E7.MirrorCS")}),1.0]])]});
            var Q30;
            {var subQ0=sQuery(id+"F0.wireOp",EDGE,"PvfX3TML-tEWY-75QP-zgdm-SnZc5ZdSM3lq");Q30=makeQuery(id+"F0.imprint","IMPRINT",FACE,{"disambiguationData":[TD([[makeQuery(id+"F0.imprint","IMPRINT",EDGE,{"derivedFrom":subQ0}),-1.0]])]});}
            var Q31;
            {var subQ0=sQuery(id+"F0.wireOp",EDGE,"VMiJEZT8-RFAT-jsT7-MDdH-zGILJkuwbvlu");Q31=makeQuery(id+"F0.imprint","IMPRINT",FACE,{"disambiguationData":[TD([[makeQuery(id+"F0.imprint","IMPRINT",EDGE,{"derivedFrom":subQ0}),-1.0]])]});}
            var Q32;
            {var subQ0=sQuery(id+"F0.wireOp",EDGE,"E43");Q32=makeQuery(id+"F0.imprint","IMPRINT",FACE,{"disambiguationData":[TD([[makeQuery(id+"F0.imprint","IMPRINT",EDGE,{"derivedFrom":subQ0}),-1.0]])]});}
            var Q33;
            {var subQ5=sQuery(id+"F0.wireOp",EDGE,"VMiJEZT8-RFAT-jsT7-MDdH-zGILJkuwbvlu");Q33=makeQuery(id+"F0.imprint","IMPRINT",FACE,{"disambiguationData":[TD([[makeQuery(id+"F0.imprint","IMPRINT",EDGE,{"derivedFrom":subQ5}),1.0]])]});}
            var Q34;
            Q34=makeQuery(id+"F0.imprint","IMPRINT",FACE,{"disambiguationData":[TD([[makeQuery(id+"F0.imprint","IMPRINT",EDGE,{"derivedFrom":sQuery(id+"F0.wireOp",EDGE,"E36")}),1.0]])]});
            var Q35;
            Q35=makeQuery(id+"F0.imprint","IMPRINT",FACE,{"disambiguationData":[TD([[makeQuery(id+"F0.imprint","IMPRINT",EDGE,{"derivedFrom":sQuery(id+"F0.wireOp",EDGE,"E37.MirrorC")}),-1.0]])]});
            var Q36;
            {var subQ4=sQuery(id+"F0.wireOp",EDGE,"E1.right");Q36=makeQuery(id+"F0.imprint","IMPRINT",FACE,{"disambiguationData":[TD([[makeQuery(id+"F0.imprint","IMPRINT",EDGE,{"derivedFrom":subQ4}),-1.0]])]});}
            var Q37;
            {var subQ1=sQuery(id+"F0.wireOp",EDGE,"VMiJEZT8-RFAT-jsT7-MDdH-zGILJkuwbvlu");var subQ9=sQuery(id+"F0.wireOp",EDGE,"E39.MirrorCS");var subQ10=makeQuery(id+"F0.imprint","INTERSECT",VERTEX,{"derivedFrom":[subQ1,subQ9]});Q37=makeQuery(id+"F0.imprint","IMPRINT",FACE,{"disambiguationData":[TD([[makeQuery(id+"F0.imprint","IMPRINT",EDGE,{"disambiguationData":[TD([[subQ10,1.0]])],"derivedFrom":subQ9}),1.0]])]});}
            var Q38;
            {var subQ0=sQuery(id+"F0.wireOp",EDGE,"E52");var subQ1=sQuery(id+"F0.wireOp",EDGE,"RdLYVHK0-ZMMy-n2T9-vo5N-ViF6aoFnglOa");var subQ2=makeQuery(id+"F0.imprint","INTERSECT",VERTEX,{"derivedFrom":[subQ1,subQ0]});Q38=makeQuery(id+"F0.imprint","IMPRINT",FACE,{"disambiguationData":[TD([[makeQuery(id+"F0.imprint","IMPRINT",EDGE,{"disambiguationData":[TD([[subQ2,-1.0]])],"derivedFrom":subQ1}),1.0]])]});}
            var Q39;
            {var subQ16=sQuery(id+"F0.wireOp",EDGE,"6d39de08-ad94-4231-b662-17a660603f591.MirrorCS");Q39=makeQuery(id+"F0.imprint","IMPRINT",FACE,{"disambiguationData":[TD([[makeQuery(id+"F0.imprint","IMPRINT",EDGE,{"derivedFrom":subQ16}),1.0]])]});}
            var Q40;
            Q40=makeQuery(id+"F0.imprint","IMPRINT",FACE,{"disambiguationData":[TD([[makeQuery(id+"F0.imprint","IMPRINT",EDGE,{"derivedFrom":sQuery(id+"F0.wireOp",EDGE,"OnmIOEd6-qnpC-QJ27-KJmg-9LLU5FsKqQjE")}),1.0]])]});
            var Q41;
            {var subQ0=sQuery(id+"F0.wireOp",EDGE,"E9.MirrorCS");Q41=makeQuery(id+"F0.imprint","IMPRINT",FACE,{"disambiguationData":[TD([[makeQuery(id+"F0.imprint","IMPRINT",EDGE,{"derivedFrom":subQ0}),1.0]])]});}
            var Q42;
            Q42=makeQuery(id+"F0.imprint","IMPRINT",FACE,{"disambiguationData":[TD([[makeQuery(id+"F0.imprint","IMPRINT",EDGE,{"derivedFrom":sQuery(id+"F0.wireOp",EDGE,"E31")}),-1.0]])]});
            var Q43;
            Q43=makeQuery(id+"F0.imprint","IMPRINT",FACE,{"disambiguationData":[TD([[makeQuery(id+"F0.imprint","IMPRINT",EDGE,{"derivedFrom":sQuery(id+"F0.wireOp",EDGE,"E0.bottom")}),-1.0]])]});
            var Q44;
            {var subQ6=sQuery(id+"F0.wireOp",EDGE,"E85");Q44=makeQuery(id+"F0.imprint","IMPRINT",FACE,{"disambiguationData":[TD([[makeQuery(id+"F0.imprint","IMPRINT",EDGE,{"derivedFrom":subQ6}),-1.0]])]});}
            var Q45;
            {var subQ0=sQuery(id+"F0.wireOp",EDGE,"E91");Q45=makeQuery(id+"F0.imprint","IMPRINT",FACE,{"disambiguationData":[TD([[makeQuery(id+"F0.imprint","IMPRINT",EDGE,{"derivedFrom":subQ0}),-1.0]])]});}
            var Q46;
            Q46=makeQuery(id+"F0.imprint","IMPRINT",FACE,{"disambiguationData":[TD([[makeQuery(id+"F0.imprint","IMPRINT",EDGE,{"derivedFrom":sQuery(id+"F0.wireOp",EDGE,"E29")}),-1.0]])]});
            var Q47;
            {var subQ0=sQuery(id+"F0.wireOp",EDGE,"E88");Q47=makeQuery(id+"F0.imprint","IMPRINT",FACE,{"disambiguationData":[TD([[makeQuery(id+"F0.imprint","IMPRINT",EDGE,{"derivedFrom":subQ0}),1.0]])]});}
            var Q48;
            {var subQ4=sQuery(id+"F0.wireOp",EDGE,"ruCD1RWU-wJnB-kggX-4DZs-hKizQa8h8jOg");Q48=makeQuery(id+"F0.imprint","IMPRINT",FACE,{"disambiguationData":[TD([[makeQuery(id+"F0.imprint","IMPRINT",EDGE,{"derivedFrom":subQ4}),-1.0]])]});}
            var Q49;
            Q49=makeQuery(id+"F0.imprint","IMPRINT",FACE,{"disambiguationData":[TD([[makeQuery(id+"F0.imprint","IMPRINT",EDGE,{"derivedFrom":sQuery(id+"F0.wireOp",EDGE,"E100")}),-1.0]])]});
            var Q50;
            Q50=makeQuery(id+"F0.imprint","IMPRINT",FACE,{"disambiguationData":[TD([[makeQuery(id+"F0.imprint","IMPRINT",EDGE,{"derivedFrom":sQuery(id+"F0.wireOp",EDGE,"IykK18Gp-FfEv-DaaX-AQvY-SuF3nASqjelH")}),1.0]])]});
            var Q51;
            Q51=makeQuery(id+"F0.imprint","IMPRINT",FACE,{"disambiguationData":[TD([[makeQuery(id+"F0.imprint","IMPRINT",EDGE,{"derivedFrom":sQuery(id+"F0.wireOp",EDGE,"96306cdb-ddaf-400d-b784-63348eaf1cb10.MirrorCS")}),-1.0]])]});
            var Q52;
            Q52=makeQuery(id+"F0.imprint","IMPRINT",FACE,{"disambiguationData":[TD([[makeQuery(id+"F0.imprint","IMPRINT",EDGE,{"derivedFrom":sQuery(id+"F0.wireOp",EDGE,"96306cdb-ddaf-400d-b784-63348eaf1cb12.MirrorC")}),-1.0]])]});
            var Q53;
            {var subQ5=sQuery(id+"F0.wireOp",EDGE,"A3f7MT6z-twOz-Xzec-rXOm-KRLiCk0BcTYY");Q53=makeQuery(id+"F0.imprint","IMPRINT",FACE,{"disambiguationData":[TD([[makeQuery(id+"F0.imprint","IMPRINT",EDGE,{"derivedFrom":subQ5}),-1.0]])]});}
            var Q54;
            Q54=makeQuery(id+"F0.imprint","IMPRINT",FACE,{"disambiguationData":[TD([[makeQuery(id+"F0.imprint","IMPRINT",EDGE,{"derivedFrom":sQuery(id+"F0.wireOp",EDGE,"4b862817-c2d6-466f-a3c4-4b251d18402a9.MirrorC")}),-1.0]])]});
            var Q55;
            {var subQ9=sQuery(id+"F0.wireOp",EDGE,"E118");Q55=makeQuery(id+"F0.imprint","IMPRINT",FACE,{"disambiguationData":[TD([[makeQuery(id+"F0.imprint","IMPRINT",EDGE,{"derivedFrom":subQ9}),-1.0]])]});}
            var Q56;
            {var subQ0=sQuery(id+"F0.wireOp",EDGE,"E98");Q56=makeQuery(id+"F0.imprint","IMPRINT",FACE,{"disambiguationData":[TD([[makeQuery(id+"F0.imprint","IMPRINT",EDGE,{"derivedFrom":subQ0}),1.0]])]});}
            var Q57;
            {var subQ5=sQuery(id+"F0.wireOp",EDGE,"E118");Q57=makeQuery(id+"F0.imprint","IMPRINT",FACE,{"disambiguationData":[TD([[makeQuery(id+"F0.imprint","IMPRINT",EDGE,{"derivedFrom":subQ5}),1.0]])]});}
            var Q58;
            Q58=makeQuery(id+"F0.imprint","IMPRINT",FACE,{"disambiguationData":[TD([[makeQuery(id+"F0.imprint","IMPRINT",EDGE,{"derivedFrom":sQuery(id+"F0.wireOp",EDGE,"5df04954-8eb5-4515-9e13-43a69edbc3d80.MirrorCS")}),-1.0]])]});
            var Q59;
            {var subQ0=sQuery(id+"F0.wireOp",EDGE,"E143");var subQ1=makeQuery(id+"F0.imprint","IMPRINT",VERTEX,{"derivedFrom":subQ0});Q59=makeQuery(id+"F0.imprint","IMPRINT",FACE,{"disambiguationData":[TD([[makeQuery(id+"F0.imprint","IMPRINT",EDGE,{"disambiguationData":[TD([[subQ1,1.0]])],"derivedFrom":subQ0}),-1.0]])]});}
            var Q60;
            {var subQ0=sQuery(id+"F0.wireOp",EDGE,"E11.MirrorCS");var subQ1=sQuery(id+"F0.wireOp",EDGE,"E3.MirrorCS");var subQ2=makeQuery(id+"F0.imprint","INTERSECT",VERTEX,{"derivedFrom":[subQ1,subQ0]});Q60=makeQuery(id+"F0.imprint","IMPRINT",FACE,{"disambiguationData":[TD([[makeQuery(id+"F0.imprint","IMPRINT",EDGE,{"disambiguationData":[TD([[subQ2,-1.0]])],"derivedFrom":subQ1}),1.0]])]});}
            var Q61;
            {var subQ0=sQuery(id+"F0.wireOp",EDGE,"E155.MirrorC");var subQ1=sQuery(id+"F0.wireOp",EDGE,"E14.left");var subQ2=makeQuery(id+"F0.imprint","INTERSECT",VERTEX,{"disambiguationData":[OD(0.0)],"derivedFrom":[subQ1,subQ0]});Q61=makeQuery(id+"F0.imprint","IMPRINT",FACE,{"disambiguationData":[TD([[makeQuery(id+"F0.imprint","IMPRINT",EDGE,{"disambiguationData":[TD([[subQ2,-1.0]])],"derivedFrom":subQ1}),-1.0]])]});}
            var Q62;
            {var subQ0=sQuery(id+"F0.wireOp",EDGE,"E155.MirrorC");var subQ1=sQuery(id+"F0.wireOp",EDGE,"E14.left");var subQ2=makeQuery(id+"F0.imprint","INTERSECT",VERTEX,{"disambiguationData":[OD(0.0)],"derivedFrom":[subQ1,subQ0]});Q62=makeQuery(id+"F0.imprint","IMPRINT",FACE,{"disambiguationData":[TD([[makeQuery(id+"F0.imprint","IMPRINT",EDGE,{"disambiguationData":[TD([[subQ2,-1.0]])],"derivedFrom":subQ1}),1.0]])]});}
            var Q63;
            {var subQ0=sQuery(id+"F0.wireOp",EDGE,"E153");var subQ1=sQuery(id+"F0.wireOp",EDGE,"E15.MirrorCS");var subQ2=makeQuery(id+"F0.imprint","INTERSECT",VERTEX,{"disambiguationData":[OD(0.0)],"derivedFrom":[subQ1,subQ0]});Q63=makeQuery(id+"F0.imprint","IMPRINT",FACE,{"disambiguationData":[TD([[makeQuery(id+"F0.imprint","IMPRINT",EDGE,{"disambiguationData":[TD([[subQ2,-1.0]])],"derivedFrom":subQ1}),1.0]])]});}
            var Q64;
            {var subQ0=sQuery(id+"F0.wireOp",EDGE,"E153");var subQ1=sQuery(id+"F0.wireOp",EDGE,"E15.MirrorCS");var subQ2=makeQuery(id+"F0.imprint","INTERSECT",VERTEX,{"disambiguationData":[OD(0.0)],"derivedFrom":[subQ1,subQ0]});Q64=makeQuery(id+"F0.imprint","IMPRINT",FACE,{"disambiguationData":[TD([[makeQuery(id+"F0.imprint","IMPRINT",EDGE,{"disambiguationData":[TD([[subQ2,-1.0]])],"derivedFrom":subQ1}),-1.0]])]});}
            var Q65;
            {var subQ8=sQuery(id+"F0.wireOp",EDGE,"E101");Q65=makeQuery(id+"F0.imprint","IMPRINT",FACE,{"disambiguationData":[TD([[makeQuery(id+"F0.imprint","IMPRINT",EDGE,{"derivedFrom":subQ8}),1.0]])]});}
            var Q66;
            {var subQ0=sQuery(id+"F0.wireOp",EDGE,"E101");Q66=makeQuery(id+"F0.imprint","IMPRINT",FACE,{"disambiguationData":[TD([[makeQuery(id+"F0.imprint","IMPRINT",EDGE,{"derivedFrom":subQ0}),-1.0]])]});}
            var Q67;
            {var subQ0=sQuery(id+"F0.wireOp",EDGE,"E140.filletArc");Q67=makeQuery(id+"F0.imprint","IMPRINT",FACE,{"disambiguationData":[TD([[makeQuery(id+"F0.imprint","IMPRINT",EDGE,{"derivedFrom":subQ0}),1.0]])]});}
            var Q68;
            {var subQ0=sQuery(id+"F0.wireOp",EDGE,"E141.filletArc");Q68=makeQuery(id+"F0.imprint","IMPRINT",FACE,{"disambiguationData":[TD([[makeQuery(id+"F0.imprint","IMPRINT",EDGE,{"derivedFrom":subQ0}),1.0]])]});}
            var Q69;
            {var subQ0=sQuery(id+"F0.wireOp",EDGE,"E149");var subQ1=sQuery(id+"F0.wireOp",EDGE,"E104");var subQ2=makeQuery(id+"F0.imprint","INTERSECT",VERTEX,{"derivedFrom":[subQ1,subQ0]});Q69=makeQuery(id+"F0.imprint","IMPRINT",FACE,{"disambiguationData":[TD([[makeQuery(id+"F0.imprint","IMPRINT",EDGE,{"disambiguationData":[TD([[subQ2,1.0]])],"derivedFrom":subQ1}),1.0]])]});}
            var Q70;
            {var subQ0=sQuery(id+"F0.wireOp",EDGE,"E161");var subQ1=sQuery(id+"F0.wireOp",EDGE,"E104");var subQ2=makeQuery(id+"F0.imprint","INTERSECT",VERTEX,{"disambiguationData":[OD(0.0)],"derivedFrom":[subQ1,subQ0]});Q70=makeQuery(id+"F0.imprint","IMPRINT",FACE,{"disambiguationData":[TD([[makeQuery(id+"F0.imprint","IMPRINT",EDGE,{"disambiguationData":[TD([[subQ2,-1.0]])],"derivedFrom":subQ1}),-1.0]])]});}
            var Q71;
            {var subQ0=sQuery(id+"F0.wireOp",EDGE,"E148");var subQ1=sQuery(id+"F0.wireOp",EDGE,"E102");var subQ2=makeQuery(id+"F0.imprint","INTERSECT",VERTEX,{"derivedFrom":[subQ1,subQ0]});Q71=makeQuery(id+"F0.imprint","IMPRINT",FACE,{"disambiguationData":[TD([[makeQuery(id+"F0.imprint","IMPRINT",EDGE,{"disambiguationData":[TD([[subQ2,1.0]])],"derivedFrom":subQ1}),-1.0]])]});}
            var Q72;
            {var subQ0=sQuery(id+"F0.wireOp",EDGE,"E161");var subQ1=sQuery(id+"F0.wireOp",EDGE,"E102");var subQ2=makeQuery(id+"F0.imprint","INTERSECT",VERTEX,{"disambiguationData":[OD(0.0)],"derivedFrom":[subQ1,subQ0]});Q72=makeQuery(id+"F0.imprint","IMPRINT",FACE,{"disambiguationData":[TD([[makeQuery(id+"F0.imprint","IMPRINT",EDGE,{"disambiguationData":[TD([[subQ2,-1.0]])],"derivedFrom":subQ1}),1.0]])]});}
            var Q73;
            {var subQ0=sQuery(id+"F0.wireOp",EDGE,"E151");var subQ1=sQuery(id+"F0.wireOp",EDGE,"E105");var subQ2=makeQuery(id+"F0.imprint","INTERSECT",VERTEX,{"derivedFrom":[subQ1,subQ0]});Q73=makeQuery(id+"F0.imprint","IMPRINT",FACE,{"disambiguationData":[TD([[makeQuery(id+"F0.imprint","IMPRINT",EDGE,{"disambiguationData":[TD([[subQ2,-1.0]])],"derivedFrom":subQ1}),-1.0]])]});}
            var Q74;
            {var subQ0=sQuery(id+"F0.wireOp",EDGE,"E161");var subQ1=sQuery(id+"F0.wireOp",EDGE,"E105");var subQ2=makeQuery(id+"F0.imprint","INTERSECT",VERTEX,{"disambiguationData":[OD(0.0)],"derivedFrom":[subQ1,subQ0]});Q74=makeQuery(id+"F0.imprint","IMPRINT",FACE,{"disambiguationData":[TD([[makeQuery(id+"F0.imprint","IMPRINT",EDGE,{"disambiguationData":[TD([[subQ2,-1.0]])],"derivedFrom":subQ1}),1.0]])]});}
            var Q75;
            {var subQ0=sQuery(id+"F0.wireOp",EDGE,"E161");var subQ1=sQuery(id+"F0.wireOp",EDGE,"E103");var subQ2=makeQuery(id+"F0.imprint","INTERSECT",VERTEX,{"disambiguationData":[OD(0.0)],"derivedFrom":[subQ1,subQ0]});Q75=makeQuery(id+"F0.imprint","IMPRINT",FACE,{"disambiguationData":[TD([[makeQuery(id+"F0.imprint","IMPRINT",EDGE,{"disambiguationData":[TD([[subQ2,-1.0]])],"derivedFrom":subQ1}),1.0]])]});}
            var Q76;
            {var subQ0=sQuery(id+"F0.wireOp",EDGE,"E150");var subQ1=sQuery(id+"F0.wireOp",EDGE,"E103");var subQ2=makeQuery(id+"F0.imprint","INTERSECT",VERTEX,{"derivedFrom":[subQ1,subQ0]});Q76=makeQuery(id+"F0.imprint","IMPRINT",FACE,{"disambiguationData":[TD([[makeQuery(id+"F0.imprint","IMPRINT",EDGE,{"disambiguationData":[TD([[subQ2,1.0]])],"derivedFrom":subQ1}),-1.0]])]});}
            var Q77;
            {var subQ1=sQuery(id+"F0.wireOp",EDGE,"E111.MirrorCS");Q77=makeQuery(id+"F0.imprint","IMPRINT",FACE,{"disambiguationData":[TD([[makeQuery(id+"F0.imprint","IMPRINT",EDGE,{"derivedFrom":subQ1}),1.0]])]});}
            var Q78;
            {var subQ4=sQuery(id+"F0.wireOp",EDGE,"E115.MirrorCS");Q78=makeQuery(id+"F0.imprint","IMPRINT",FACE,{"disambiguationData":[TD([[makeQuery(id+"F0.imprint","IMPRINT",EDGE,{"derivedFrom":subQ4}),1.0]])]});}
            var Q79;
            {var subQ0=sQuery(id+"F0.wireOp",EDGE,"E111.MirrorCS");Q79=makeQuery(id+"F0.imprint","IMPRINT",FACE,{"disambiguationData":[TD([[makeQuery(id+"F0.imprint","IMPRINT",EDGE,{"derivedFrom":subQ0}),-1.0]])]});}
            var Q80;
            {var subQ1=sQuery(id+"F0.wireOp",EDGE,"E112.MirrorCS");Q80=makeQuery(id+"F0.imprint","IMPRINT",FACE,{"disambiguationData":[TD([[makeQuery(id+"F0.imprint","IMPRINT",EDGE,{"derivedFrom":subQ1}),-1.0]])]});}
            var Q81;
            {var subQ2=sQuery(id+"F0.wireOp",EDGE,"6d39de08-ad94-4231-b662-17a660603f595.MirrorCS");Q81=makeQuery(id+"F0.imprint","IMPRINT",FACE,{"disambiguationData":[TD([[makeQuery(id+"F0.imprint","IMPRINT",EDGE,{"derivedFrom":subQ2}),1.0]])]});}
            var Q82;
            {var subQ11=sQuery(id+"F0.wireOp",EDGE,"E168");Q82=makeQuery(id+"F0.imprint","IMPRINT",FACE,{"disambiguationData":[TD([[makeQuery(id+"F0.imprint","IMPRINT",EDGE,{"derivedFrom":subQ11}),-1.0]])]});}
            var Q83;
            {var subQ0=sQuery(id+"F0.wireOp",EDGE,"E170");Q83=makeQuery(id+"F0.imprint","IMPRINT",FACE,{"disambiguationData":[TD([[makeQuery(id+"F0.imprint","IMPRINT",EDGE,{"derivedFrom":subQ0}),-1.0]])]});}
            var Q84;
            {var subQ12=sQuery(id+"F0.wireOp",EDGE,"6d39de08-ad94-4231-b662-17a660603f597.MirrorCS");Q84=makeQuery(id+"F0.imprint","IMPRINT",FACE,{"disambiguationData":[TD([[makeQuery(id+"F0.imprint","IMPRINT",EDGE,{"derivedFrom":subQ12}),-1.0]])]});}
            var Q85;
            {var subQ0=sQuery(id+"F0.wireOp",EDGE,"E174.MirrorCS");Q85=makeQuery(id+"F0.imprint","IMPRINT",FACE,{"disambiguationData":[TD([[makeQuery(id+"F0.imprint","IMPRINT",EDGE,{"derivedFrom":subQ0}),1.0]])]});}
            var Q86;
            {var subQ0=sQuery(id+"F0.wireOp",EDGE,"E184");Q86=makeQuery(id+"F0.imprint","IMPRINT",FACE,{"disambiguationData":[TD([[makeQuery(id+"F0.imprint","IMPRINT",EDGE,{"derivedFrom":subQ0}),-1.0]])]});}
            var Q87;
            {var subQ6=sQuery(id+"F0.wireOp",EDGE,"E39.MirrorCS");Q87=makeQuery(id+"F0.imprint","IMPRINT",FACE,{"disambiguationData":[TD([[makeQuery(id+"F0.imprint","IMPRINT",EDGE,{"derivedFrom":subQ6}),-1.0]])]});}
            var Q88;
            {var subQ5=sQuery(id+"F0.wireOp",EDGE,"E44");Q88=makeQuery(id+"F0.imprint","IMPRINT",FACE,{"disambiguationData":[TD([[makeQuery(id+"F0.imprint","IMPRINT",EDGE,{"derivedFrom":subQ5}),-1.0]])]});}
            var Q89;
            Q89=makeQuery(id+"F0.imprint","IMPRINT",FACE,{"disambiguationData":[TD([[makeQuery(id+"F0.imprint","IMPRINT",EDGE,{"derivedFrom":sQuery(id+"F0.wireOp",EDGE,"E190.MirrorCS")}),1.0]])]});
            var Q90;
            {var subQ0=sQuery(id+"F0.wireOp",EDGE,"E199.MirrorCS");Q90=makeQuery(id+"F0.imprint","IMPRINT",FACE,{"disambiguationData":[TD([[makeQuery(id+"F0.imprint","IMPRINT",EDGE,{"derivedFrom":subQ0}),1.0]])]});}
            var Q91;
            {var subQ3=sQuery(id+"F0.wireOp",EDGE,"E191.MirrorCS");Q91=makeQuery(id+"F0.imprint","IMPRINT",FACE,{"disambiguationData":[TD([[makeQuery(id+"F0.imprint","IMPRINT",EDGE,{"derivedFrom":subQ3}),1.0]])]});}
            var Q92;
            {var subQ0=sQuery(id+"F0.wireOp",EDGE,"a47eecba-8c5f-4a7c-900a-808ab747d87a.filletArc");Q92=makeQuery(id+"F0.imprint","IMPRINT",FACE,{"disambiguationData":[TD([[makeQuery(id+"F0.imprint","IMPRINT",EDGE,{"derivedFrom":subQ0}),1.0]])]});}
            var Q93;
            {var subQ0=sQuery(id+"F0.wireOp",EDGE,"0f396da1-d1f9-489b-bf06-9032d38e7eba");var subQ1=sQuery(id+"F0.wireOp",EDGE,"394efb8b-a457-4a09-927e-0cca3ccec720");var subQ2=makeQuery(id+"F0.imprint","INTERSECT",VERTEX,{"derivedFrom":[subQ1,subQ0]});Q93=makeQuery(id+"F0.imprint","IMPRINT",FACE,{"disambiguationData":[TD([[makeQuery(id+"F0.imprint","IMPRINT",EDGE,{"disambiguationData":[TD([[subQ2,1.0]])],"derivedFrom":subQ1}),-1.0]])]});}
            var Q94;
            {var subQ0=sQuery(id+"F0.wireOp",EDGE,"H7Zu6mcE-TzpD-Prs2-afAv-bb7UNrpKUnZ3");var subQ1=sQuery(id+"F0.wireOp",EDGE,"394efb8b-a457-4a09-927e-0cca3ccec720");var subQ2=makeQuery(id+"F0.imprint","INTERSECT",VERTEX,{"disambiguationData":[OD(0.0)],"derivedFrom":[subQ1,subQ0]});Q94=makeQuery(id+"F0.imprint","IMPRINT",FACE,{"disambiguationData":[TD([[makeQuery(id+"F0.imprint","IMPRINT",EDGE,{"disambiguationData":[TD([[subQ2,-1.0]])],"derivedFrom":subQ1}),1.0]])]});}
            var Q95;
            {var subQ0=sQuery(id+"F0.wireOp",EDGE,"1e5f49b8-77da-43ca-8d71-619981cc3dd5.filletArc");Q95=makeQuery(id+"F0.imprint","IMPRINT",FACE,{"disambiguationData":[TD([[makeQuery(id+"F0.imprint","IMPRINT",EDGE,{"derivedFrom":subQ0}),1.0]])]});}
            var Q96;
            {var subQ0=sQuery(id+"F0.wireOp",EDGE,"2953cc8a-75ce-4042-964e-4aa7a04384ec0.MirrorCS");var subQ1=sQuery(id+"F0.wireOp",EDGE,"62e97f5a-d78d-431a-af55-523a3b282b310.MirrorCS");var subQ2=makeQuery(id+"F0.imprint","INTERSECT",VERTEX,{"derivedFrom":[subQ1,subQ0]});Q96=makeQuery(id+"F0.imprint","IMPRINT",FACE,{"disambiguationData":[TD([[makeQuery(id+"F0.imprint","IMPRINT",EDGE,{"disambiguationData":[TD([[subQ2,-1.0]])],"derivedFrom":subQ1}),1.0]])]});}
            var Q97;
            {var subQ0=sQuery(id+"F0.wireOp",EDGE,"5df04954-8eb5-4515-9e13-43a69edbc3d89.MirrorCS");var subQ1=sQuery(id+"F0.wireOp",EDGE,"5df04954-8eb5-4515-9e13-43a69edbc3d83.MirrorCS");var subQ2=makeQuery(id+"F0.imprint","INTERSECT",VERTEX,{"derivedFrom":[subQ1,subQ0]});Q97=makeQuery(id+"F0.imprint","IMPRINT",FACE,{"disambiguationData":[TD([[makeQuery(id+"F0.imprint","IMPRINT",EDGE,{"disambiguationData":[TD([[subQ2,1.0]])],"derivedFrom":subQ1}),1.0]])]});}
            var Q98;
            {var subQ0=sQuery(id+"F0.wireOp",EDGE,"7baa0f8b-bd87-4a79-816f-f555f1973061");Q98=makeQuery(id+"F0.imprint","IMPRINT",FACE,{"disambiguationData":[TD([[makeQuery(id+"F0.imprint","IMPRINT",EDGE,{"derivedFrom":subQ0}),-1.0]])]});}
            var Q99;
            {var subQ0=sQuery(id+"F0.wireOp",EDGE,"1e7b46df-daae-406a-85df-c87a7ed3f0fb");Q99=makeQuery(id+"F0.imprint","IMPRINT",FACE,{"disambiguationData":[TD([[makeQuery(id+"F0.imprint","IMPRINT",EDGE,{"derivedFrom":subQ0}),1.0]])]});}
            var Q100;
            Q100=makeQuery(id+"F0.imprint","IMPRINT",FACE,{"disambiguationData":[TD([[makeQuery(id+"F0.imprint","IMPRINT",EDGE,{"derivedFrom":sQuery(id+"F0.wireOp",EDGE,"E224")}),-1.0]])]});
            var Q101;
            Q101=makeQuery(id+"F0.imprint","IMPRINT",FACE,{"disambiguationData":[TD([[makeQuery(id+"F0.imprint","IMPRINT",EDGE,{"derivedFrom":sQuery(id+"F0.wireOp",EDGE,"E226.MirrorC")}),-1.0]])]});
            extrude(context, id + "F1", {"entities" : qUnion([Q0, Q1, Q2, Q3, Q4, Q5, Q6, Q7, Q8, Q9, Q10, Q11, Q12, Q13, Q14, Q15, Q16, Q17, Q18, Q19, Q20, Q21, Q22, Q23, Q24, Q25, Q26, Q27, Q28, Q29, Q30, Q31, Q32, Q33, Q34, Q35, Q36, Q37, Q38, Q39, Q40, Q41, Q42, Q43, Q44, Q45, Q46, Q47, Q48, Q49, Q50, Q51, Q52, Q53, Q54, Q55, Q56, Q57, Q58, Q59, Q60, Q61, Q62, Q63, Q64, Q65, Q66, Q67, Q68, Q69, Q70, Q71, Q72, Q73, Q74, Q75, Q76, Q77, Q78, Q79, Q80, Q81, Q82, Q83, Q84, Q85, Q86, Q87, Q88, Q89, Q90, Q91, Q92, Q93, Q94, Q95, Q96, Q97, Q98, Q99, Q100, Q101]), "oppositeDirection" : true, "depth" : 30 * mm, "offsetDistance" : 25 * mm});
        }
        {
            var Q0;
            {var subQ5=sQuery(id+"F0.wireOp",EDGE,"VMiJEZT8-RFAT-jsT7-MDdH-zGILJkuwbvlu");Q0=makeQuery(id+"F0.imprint","IMPRINT",FACE,{"disambiguationData":[TD([[makeQuery(id+"F0.imprint","IMPRINT",EDGE,{"derivedFrom":subQ5}),1.0]])]});}
            var Q1;
            Q1=makeQuery(id+"F0.imprint","IMPRINT",FACE,{"disambiguationData":[TD([[makeQuery(id+"F0.imprint","IMPRINT",EDGE,{"derivedFrom":sQuery(id+"F0.wireOp",EDGE,"OnmIOEd6-qnpC-QJ27-KJmg-9LLU5FsKqQjE")}),1.0]])]});
            var Q2;
            {var subQ0=sQuery(id+"F0.wireOp",EDGE,"E9.MirrorCS");Q2=makeQuery(id+"F0.imprint","IMPRINT",FACE,{"disambiguationData":[TD([[makeQuery(id+"F0.imprint","IMPRINT",EDGE,{"derivedFrom":subQ0}),1.0]])]});}
            var Q3;
            {var subQ0=sQuery(id+"F0.wireOp",EDGE,"VMiJEZT8-RFAT-jsT7-MDdH-zGILJkuwbvlu");var subQ1=sQuery(id+"F0.wireOp",EDGE,"E2.left");var subQ2=makeQuery(id+"F0.imprint","INTERSECT",VERTEX,{"derivedFrom":[subQ1,subQ0]});Q3=makeQuery(id+"F0.imprint","IMPRINT",FACE,{"disambiguationData":[TD([[makeQuery(id+"F0.imprint","IMPRINT",EDGE,{"disambiguationData":[TD([[subQ2,-1.0]])],"derivedFrom":subQ1}),-1.0]])]});}
            var Q4;
            {var subQ4=sQuery(id+"F0.wireOp",EDGE,"E1.right");Q4=makeQuery(id+"F0.imprint","IMPRINT",FACE,{"disambiguationData":[TD([[makeQuery(id+"F0.imprint","IMPRINT",EDGE,{"derivedFrom":subQ4}),-1.0]])]});}
            var Q5;
            Q5=makeQuery(id+"F0.imprint","IMPRINT",FACE,{"disambiguationData":[TD([[makeQuery(id+"F0.imprint","IMPRINT",EDGE,{"derivedFrom":sQuery(id+"F0.wireOp",EDGE,"E31")}),-1.0]])]});
            var Q6;
            {var subQ16=sQuery(id+"F0.wireOp",EDGE,"6d39de08-ad94-4231-b662-17a660603f591.MirrorCS");Q6=makeQuery(id+"F0.imprint","IMPRINT",FACE,{"disambiguationData":[TD([[makeQuery(id+"F0.imprint","IMPRINT",EDGE,{"derivedFrom":subQ16}),1.0]])]});}
            var Q7;
            Q7=makeQuery(id+"F0.imprint","IMPRINT",FACE,{"disambiguationData":[TD([[makeQuery(id+"F0.imprint","IMPRINT",EDGE,{"derivedFrom":sQuery(id+"F0.wireOp",EDGE,"E7.MirrorCS")}),1.0]])]});
            var Q8;
            {var subQ5=sQuery(id+"F0.wireOp",EDGE,"E89");Q8=makeQuery(id+"F0.imprint","IMPRINT",FACE,{"disambiguationData":[TD([[makeQuery(id+"F0.imprint","IMPRINT",EDGE,{"derivedFrom":subQ5}),-1.0]])]});}
            var Q9;
            {var subQ0=sQuery(id+"F0.wireOp",EDGE,"E91");Q9=makeQuery(id+"F0.imprint","IMPRINT",FACE,{"disambiguationData":[TD([[makeQuery(id+"F0.imprint","IMPRINT",EDGE,{"derivedFrom":subQ0}),-1.0]])]});}
            var Q10;
            Q10=makeQuery(id+"F0.imprint","IMPRINT",FACE,{"disambiguationData":[TD([[makeQuery(id+"F0.imprint","IMPRINT",EDGE,{"derivedFrom":sQuery(id+"F0.wireOp",EDGE,"96306cdb-ddaf-400d-b784-63348eaf1cb10.MirrorCS")}),-1.0]])]});
            var Q11;
            Q11=makeQuery(id+"F0.imprint","IMPRINT",FACE,{"disambiguationData":[TD([[makeQuery(id+"F0.imprint","IMPRINT",EDGE,{"derivedFrom":sQuery(id+"F0.wireOp",EDGE,"E100")}),-1.0]])]});
            var Q12;
            Q12=makeQuery(id+"F0.imprint","IMPRINT",FACE,{"disambiguationData":[TD([[makeQuery(id+"F0.imprint","IMPRINT",EDGE,{"derivedFrom":sQuery(id+"F0.wireOp",EDGE,"4b862817-c2d6-466f-a3c4-4b251d18402a9.MirrorC")}),-1.0]])]});
            var Q13;
            Q13=makeQuery(id+"F0.imprint","IMPRINT",FACE,{"disambiguationData":[TD([[makeQuery(id+"F0.imprint","IMPRINT",EDGE,{"derivedFrom":sQuery(id+"F0.wireOp",EDGE,"IykK18Gp-FfEv-DaaX-AQvY-SuF3nASqjelH")}),1.0]])]});
            var Q14;
            {var subQ0=sQuery(id+"F0.wireOp",EDGE,"E111.MirrorCS");Q14=makeQuery(id+"F0.imprint","IMPRINT",FACE,{"disambiguationData":[TD([[makeQuery(id+"F0.imprint","IMPRINT",EDGE,{"derivedFrom":subQ0}),-1.0]])]});}
            var Q15;
            {var subQ1=sQuery(id+"F0.wireOp",EDGE,"E111.MirrorCS");Q15=makeQuery(id+"F0.imprint","IMPRINT",FACE,{"disambiguationData":[TD([[makeQuery(id+"F0.imprint","IMPRINT",EDGE,{"derivedFrom":subQ1}),1.0]])]});}
            var Q16;
            {var subQ8=sQuery(id+"F0.wireOp",EDGE,"E101");Q16=makeQuery(id+"F0.imprint","IMPRINT",FACE,{"disambiguationData":[TD([[makeQuery(id+"F0.imprint","IMPRINT",EDGE,{"derivedFrom":subQ8}),1.0]])]});}
            var Q17;
            {var subQ0=sQuery(id+"F0.wireOp",EDGE,"E101");Q17=makeQuery(id+"F0.imprint","IMPRINT",FACE,{"disambiguationData":[TD([[makeQuery(id+"F0.imprint","IMPRINT",EDGE,{"derivedFrom":subQ0}),-1.0]])]});}
            var Q18;
            {var subQ5=sQuery(id+"F0.wireOp",EDGE,"E44");Q18=makeQuery(id+"F0.imprint","IMPRINT",FACE,{"disambiguationData":[TD([[makeQuery(id+"F0.imprint","IMPRINT",EDGE,{"derivedFrom":subQ5}),-1.0]])]});}
            var Q19;
            {var subQ6=sQuery(id+"F0.wireOp",EDGE,"E39.MirrorCS");Q19=makeQuery(id+"F0.imprint","IMPRINT",FACE,{"disambiguationData":[TD([[makeQuery(id+"F0.imprint","IMPRINT",EDGE,{"derivedFrom":subQ6}),-1.0]])]});}
            var Q20;
            Q20=makeQuery(id+"F0.imprint","IMPRINT",FACE,{"disambiguationData":[TD([[makeQuery(id+"F0.imprint","IMPRINT",EDGE,{"derivedFrom":sQuery(id+"F0.wireOp",EDGE,"E32")}),-1.0]])]});
            var Q21;
            {var subQ0=sQuery(id+"F0.wireOp",EDGE,"7baa0f8b-bd87-4a79-816f-f555f1973061");Q21=makeQuery(id+"F0.imprint","IMPRINT",FACE,{"disambiguationData":[TD([[makeQuery(id+"F0.imprint","IMPRINT",EDGE,{"derivedFrom":subQ0}),-1.0]])]});}
            var Q22;
            {var subQ0=sQuery(id+"F0.wireOp",EDGE,"0f396da1-d1f9-489b-bf06-9032d38e7eba");var subQ1=sQuery(id+"F0.wireOp",EDGE,"394efb8b-a457-4a09-927e-0cca3ccec720");var subQ2=makeQuery(id+"F0.imprint","INTERSECT",VERTEX,{"derivedFrom":[subQ1,subQ0]});Q22=makeQuery(id+"F0.imprint","IMPRINT",FACE,{"disambiguationData":[TD([[makeQuery(id+"F0.imprint","IMPRINT",EDGE,{"disambiguationData":[TD([[subQ2,1.0]])],"derivedFrom":subQ1}),-1.0]])]});}
            var Q23;
            {var subQ0=sQuery(id+"F0.wireOp",EDGE,"1e5f49b8-77da-43ca-8d71-619981cc3dd5.filletArc");Q23=makeQuery(id+"F0.imprint","IMPRINT",FACE,{"disambiguationData":[TD([[makeQuery(id+"F0.imprint","IMPRINT",EDGE,{"derivedFrom":subQ0}),1.0]])]});}
            var Q24;
            {var subQ0=sQuery(id+"F0.wireOp",EDGE,"2953cc8a-75ce-4042-964e-4aa7a04384ec0.MirrorCS");var subQ1=sQuery(id+"F0.wireOp",EDGE,"62e97f5a-d78d-431a-af55-523a3b282b310.MirrorCS");var subQ2=makeQuery(id+"F0.imprint","INTERSECT",VERTEX,{"derivedFrom":[subQ1,subQ0]});Q24=makeQuery(id+"F0.imprint","IMPRINT",FACE,{"disambiguationData":[TD([[makeQuery(id+"F0.imprint","IMPRINT",EDGE,{"disambiguationData":[TD([[subQ2,-1.0]])],"derivedFrom":subQ1}),1.0]])]});}
            var Q25;
            Q25=makeQuery(id+"F1.opExtrude","CAP_FACE",FACE,{"disambiguationData":[OSD([sQuery(id+"F0.wireOp",EDGE,"E0.bottom"),sQuery(id+"F0.wireOp",EDGE,"E0.right"),sQuery(id+"F0.wireOp",EDGE,"E1.bottom"),sQuery(id+"F0.wireOp",EDGE,"E1.left"),sQuery(id+"F0.wireOp",EDGE,"E3.MirrorCS"),sQuery(id+"F0.wireOp",EDGE,"E4.MirrorCS"),sQuery(id+"F0.wireOp",EDGE,"E5.MirrorCS"),sQuery(id+"F0.wireOp",EDGE,"E6.MirrorCS"),sQuery(id+"F0.wireOp",EDGE,"E8.MirrorCS"),sQuery(id+"F0.wireOp",EDGE,"E10.MirrorCS"),sQuery(id+"F0.wireOp",EDGE,"E12"),sQuery(id+"F0.wireOp",EDGE,"E13"),sQuery(id+"F0.wireOp",EDGE,"E25"),sQuery(id+"F0.wireOp",EDGE,"E26"),sQuery(id+"F0.wireOp",EDGE,"E27"),sQuery(id+"F0.wireOp",EDGE,"E28"),sQuery(id+"F0.wireOp",EDGE,"E46"),sQuery(id+"F0.wireOp",EDGE,"E66.filletArc"),sQuery(id+"F0.wireOp",EDGE,"E67.filletArc"),sQuery(id+"F0.wireOp",EDGE,"E74.filletArc"),sQuery(id+"F0.wireOp",EDGE,"E75.filletArc"),sQuery(id+"F0.wireOp",EDGE,"E85"),sQuery(id+"F0.wireOp",EDGE,"1e7b46df-daae-406a-85df-c87a7ed3f0fb"),sQuery(id+"F0.wireOp",EDGE,"7baa0f8b-bd87-4a79-816f-f555f1973061"),sQuery(id+"F0.wireOp",EDGE,"394efb8b-a457-4a09-927e-0cca3ccec720"),sQuery(id+"F0.wireOp",EDGE,"9dbf79d4-462b-4309-af9a-ff4caacc0494"),sQuery(id+"F0.wireOp",EDGE,"f532204f-58c9-45fd-867f-38ba44cf0707"),sQuery(id+"F0.wireOp",EDGE,"acf12cf6-cf0c-4576-b312-3182e6e53ff6"),sQuery(id+"F0.wireOp",EDGE,"0f396da1-d1f9-489b-bf06-9032d38e7eba"),sQuery(id+"F0.wireOp",EDGE,"b732a203-f060-4852-94d0-d5c29e6ce8c8"),sQuery(id+"F0.wireOp",EDGE,"5df04954-8eb5-4515-9e13-43a69edbc3d82.MirrorCS"),sQuery(id+"F0.wireOp",EDGE,"5df04954-8eb5-4515-9e13-43a69edbc3d84.MirrorCS"),sQuery(id+"F0.wireOp",EDGE,"5df04954-8eb5-4515-9e13-43a69edbc3d85.MirrorCS"),sQuery(id+"F0.wireOp",EDGE,"5df04954-8eb5-4515-9e13-43a69edbc3d87.MirrorCS"),sQuery(id+"F0.wireOp",EDGE,"5df04954-8eb5-4515-9e13-43a69edbc3d88.MirrorCS"),sQuery(id+"F0.wireOp",EDGE,"5df04954-8eb5-4515-9e13-43a69edbc3d89.MirrorCS"),sQuery(id+"F0.wireOp",EDGE,"5df04954-8eb5-4515-9e13-43a69edbc3d810.MirrorCS"),sQuery(id+"F0.wireOp",EDGE,"5df04954-8eb5-4515-9e13-43a69edbc3d812.MirrorCS"),sQuery(id+"F0.wireOp",EDGE,"E160"),sQuery(id+"F0.wireOp",EDGE,"E162"),sQuery(id+"F0.wireOp",EDGE,"2953cc8a-75ce-4042-964e-4aa7a04384ec0.MirrorCS"),sQuery(id+"F0.wireOp",EDGE,"E194.MirrorCS"),sQuery(id+"F0.wireOp",EDGE,"E196.MirrorCS"),sQuery(id+"F0.wireOp",EDGE,"E197.MirrorCS"),sQuery(id+"F0.wireOp",EDGE,"E201.MirrorCS"),sQuery(id+"F0.wireOp",EDGE,"E203.MirrorCS"),sQuery(id+"F0.wireOp",EDGE,"E204.MirrorCS"),sQuery(id+"F0.wireOp",EDGE,"E205.MirrorCS"),sQuery(id+"F0.wireOp",EDGE,"E208.MirrorCS"),sQuery(id+"F0.wireOp",EDGE,"H7Zu6mcE-TzpD-Prs2-afAv-bb7UNrpKUnZ3"),sQuery(id+"F0.wireOp",EDGE,"Sv7zSBnD-SEQH-Q2nj-tlxK-Q70GRJM5dvfs")])],"isStart":false});
            extrude(context, id + "F2", {"entities" : qUnion([Q0, Q1, Q2, Q3, Q4, Q5, Q6, Q7, Q8, Q9, Q10, Q11, Q12, Q13, Q14, Q15, Q16, Q17, Q18, Q19, Q20, Q21, Q22, Q23, Q24, Q25]), "operationType" : NewBodyOperationType.REMOVE, "oppositeDirection" : true, "depth" : 30 * mm, "offsetDistance" : 25 * mm, "hasSecondDirection" : true, "secondDirectionOppositeDirection" : true, "secondDirectionDepth" : 12 * mm});
        }
        {
            var Q0;
            {var subQ11=sQuery(id+"F0.wireOp",EDGE,"E168");Q0=makeQuery(id+"F0.imprint","IMPRINT",FACE,{"disambiguationData":[TD([[makeQuery(id+"F0.imprint","IMPRINT",EDGE,{"derivedFrom":subQ11}),-1.0]])]});}
            var Q1;
            {var subQ0=sQuery(id+"F0.wireOp",EDGE,"E170");Q1=makeQuery(id+"F0.imprint","IMPRINT",FACE,{"disambiguationData":[TD([[makeQuery(id+"F0.imprint","IMPRINT",EDGE,{"derivedFrom":subQ0}),-1.0]])]});}
            var Q2;
            {var subQ7=sQuery(id+"F0.wireOp",EDGE,"E167");Q2=makeQuery(id+"F0.imprint","IMPRINT",FACE,{"disambiguationData":[TD([[makeQuery(id+"F0.imprint","IMPRINT",EDGE,{"derivedFrom":subQ7}),-1.0]])]});}
            var Q3;
            {var subQ0=sQuery(id+"F0.wireOp",EDGE,"E174.MirrorCS");Q3=makeQuery(id+"F0.imprint","IMPRINT",FACE,{"disambiguationData":[TD([[makeQuery(id+"F0.imprint","IMPRINT",EDGE,{"derivedFrom":subQ0}),1.0]])]});}
            var Q4;
            Q4=makeQuery(id+"F0.imprint","IMPRINT",FACE,{"disambiguationData":[TD([[makeQuery(id+"F0.imprint","IMPRINT",EDGE,{"derivedFrom":sQuery(id+"F0.wireOp",EDGE,"E27")}),-1.0]])]});
            var Q5;
            Q5=makeQuery(id+"F0.imprint","IMPRINT",FACE,{"disambiguationData":[TD([[makeQuery(id+"F0.imprint","IMPRINT",EDGE,{"derivedFrom":sQuery(id+"F0.wireOp",EDGE,"E7.MirrorCS")}),-1.0]])]});
            var Q6;
            Q6=makeQuery(id+"F0.imprint","IMPRINT",FACE,{"disambiguationData":[TD([[makeQuery(id+"F0.imprint","IMPRINT",EDGE,{"derivedFrom":sQuery(id+"F0.wireOp",EDGE,"E59.MirrorC")}),1.0]])]});
            var Q7;
            Q7=makeQuery(id+"F0.imprint","IMPRINT",FACE,{"disambiguationData":[TD([[makeQuery(id+"F0.imprint","IMPRINT",EDGE,{"derivedFrom":sQuery(id+"F0.wireOp",EDGE,"E37.MirrorC")}),1.0]])]});
            var Q8;
            Q8=makeQuery(id+"F0.imprint","IMPRINT",FACE,{"disambiguationData":[TD([[makeQuery(id+"F0.imprint","IMPRINT",EDGE,{"derivedFrom":sQuery(id+"F0.wireOp",EDGE,"e0f77c02-860a-4edd-adaa-7ff4540aa646.filletArc")}),-1.0]])]});
            var Q9;
            Q9=makeQuery(id+"F0.imprint","IMPRINT",FACE,{"disambiguationData":[TD([[makeQuery(id+"F0.imprint","IMPRINT",EDGE,{"derivedFrom":sQuery(id+"F0.wireOp",EDGE,"E190.MirrorCS")}),1.0]])]});
            var Q10;
            {var subQ3=sQuery(id+"F0.wireOp",EDGE,"E191.MirrorCS");Q10=makeQuery(id+"F0.imprint","IMPRINT",FACE,{"disambiguationData":[TD([[makeQuery(id+"F0.imprint","IMPRINT",EDGE,{"derivedFrom":subQ3}),1.0]])]});}
            var Q11;
            Q11=makeQuery(id+"F0.imprint","IMPRINT",FACE,{"disambiguationData":[TD([[makeQuery(id+"F0.imprint","IMPRINT",EDGE,{"derivedFrom":sQuery(id+"F0.wireOp",EDGE,"E37.MirrorC")}),-1.0]])]});
            var Q12;
            Q12=makeQuery(id+"F0.imprint","IMPRINT",FACE,{"disambiguationData":[TD([[makeQuery(id+"F0.imprint","IMPRINT",EDGE,{"derivedFrom":sQuery(id+"F0.wireOp",EDGE,"E36")}),-1.0]])]});
            var Q13;
            Q13=makeQuery(id+"F0.imprint","IMPRINT",FACE,{"disambiguationData":[TD([[makeQuery(id+"F0.imprint","IMPRINT",EDGE,{"derivedFrom":sQuery(id+"F0.wireOp",EDGE,"E36")}),1.0]])]});
            var Q14;
            Q14=makeQuery(id+"F0.imprint","IMPRINT",FACE,{"disambiguationData":[TD([[makeQuery(id+"F0.imprint","IMPRINT",EDGE,{"derivedFrom":sQuery(id+"F0.wireOp",EDGE,"E59.MirrorC")}),-1.0]])]});
            var Q15;
            {var subQ0=sQuery(id+"F0.wireOp",EDGE,"E43");Q15=makeQuery(id+"F0.imprint","IMPRINT",FACE,{"disambiguationData":[TD([[makeQuery(id+"F0.imprint","IMPRINT",EDGE,{"derivedFrom":subQ0}),1.0]])]});}
            var Q16;
            {var subQ5=sQuery(id+"F0.wireOp",EDGE,"E89");Q16=makeQuery(id+"F0.imprint","IMPRINT",FACE,{"disambiguationData":[TD([[makeQuery(id+"F0.imprint","IMPRINT",EDGE,{"derivedFrom":subQ5}),-1.0]])]});}
            var Q17;
            Q17=makeQuery(id+"F0.imprint","IMPRINT",FACE,{"disambiguationData":[TD([[makeQuery(id+"F0.imprint","IMPRINT",EDGE,{"derivedFrom":sQuery(id+"F0.wireOp",EDGE,"E226.MirrorC")}),-1.0]])]});
            var Q18;
            Q18=makeQuery(id+"F0.imprint","IMPRINT",FACE,{"disambiguationData":[TD([[makeQuery(id+"F0.imprint","IMPRINT",EDGE,{"derivedFrom":sQuery(id+"F0.wireOp",EDGE,"E224")}),-1.0]])]});
            var Q19;
            {var subQ2=sQuery(id+"F0.wireOp",EDGE,"E91");Q19=makeQuery(id+"F0.imprint","IMPRINT",FACE,{"disambiguationData":[TD([[makeQuery(id+"F0.imprint","IMPRINT",EDGE,{"derivedFrom":subQ2}),-1.0]])]});}
            extrude(context, id + "F3", {"entities" : qUnion([Q0, Q1, Q2, Q3, Q4, Q5, Q6, Q7, Q8, Q9, Q10, Q11, Q12, Q13, Q14, Q15, Q16, Q17, Q18, Q19]), "operationType" : NewBodyOperationType.REMOVE, "oppositeDirection" : true, "depth" : 30 * mm, "offsetDistance" : 25 * mm, "hasSecondDirection" : true, "secondDirectionOppositeDirection" : true, "secondDirectionDepth" : 3 * mm});
        }
        {
            var Q0;
            {var subQ3=sQuery(id+"F0.wireOp",EDGE,"539c7ef6-e73b-46dd-b7a3-ca27ce5554f6.filletArc");Q0=makeQuery(id+"F0.imprint","IMPRINT",FACE,{"disambiguationData":[TD([[makeQuery(id+"F0.imprint","IMPRINT",EDGE,{"derivedFrom":subQ3}),-1.0]])]});}
            var Q1;
            {var subQ3=sQuery(id+"F0.wireOp",EDGE,"12c242b3-208e-4177-b4b7-cfe86d31bad3.filletArc");Q1=makeQuery(id+"F0.imprint","IMPRINT",FACE,{"disambiguationData":[TD([[makeQuery(id+"F0.imprint","IMPRINT",EDGE,{"derivedFrom":subQ3}),-1.0]])]});}
            var Q2;
            {var subQ6=sQuery(id+"F0.wireOp",EDGE,"E40");Q2=makeQuery(id+"F0.imprint","IMPRINT",FACE,{"disambiguationData":[TD([[makeQuery(id+"F0.imprint","IMPRINT",EDGE,{"derivedFrom":subQ6}),-1.0]])]});}
            var Q3;
            Q3=makeQuery(id+"F0.imprint","IMPRINT",FACE,{"disambiguationData":[TD([[makeQuery(id+"F0.imprint","IMPRINT",EDGE,{"derivedFrom":sQuery(id+"F0.wireOp",EDGE,"E29")}),-1.0]])]});
            var Q4;
            {var subQ7=sQuery(id+"F0.wireOp",EDGE,"E39.MirrorCS");Q4=makeQuery(id+"F0.imprint","IMPRINT",FACE,{"disambiguationData":[TD([[makeQuery(id+"F0.imprint","IMPRINT",EDGE,{"derivedFrom":subQ7}),1.0]])]});}
            var Q5;
            {var subQ0=sQuery(id+"F0.wireOp",EDGE,"E43");Q5=makeQuery(id+"F0.imprint","IMPRINT",FACE,{"disambiguationData":[TD([[makeQuery(id+"F0.imprint","IMPRINT",EDGE,{"derivedFrom":subQ0}),-1.0]])]});}
            var Q6;
            {var subQ0=sQuery(id+"F0.wireOp",EDGE,"Sg2hh5cT-w1Nn-jAqg-wGWI-78aZj25IGyF1");Q6=makeQuery(id+"F0.imprint","IMPRINT",FACE,{"disambiguationData":[TD([[makeQuery(id+"F0.imprint","IMPRINT",EDGE,{"derivedFrom":subQ0}),1.0]])]});}
            var Q7;
            {var subQ1=sQuery(id+"F0.wireOp",EDGE,"Sg2hh5cT-w1Nn-jAqg-wGWI-78aZj25IGyF1");Q7=makeQuery(id+"F0.imprint","IMPRINT",FACE,{"disambiguationData":[TD([[makeQuery(id+"F0.imprint","IMPRINT",EDGE,{"derivedFrom":subQ1}),-1.0]])]});}
            var Q8;
            {var subQ2=sQuery(id+"F0.wireOp",EDGE,"E88");Q8=makeQuery(id+"F0.imprint","IMPRINT",FACE,{"disambiguationData":[TD([[makeQuery(id+"F0.imprint","IMPRINT",EDGE,{"derivedFrom":subQ2}),-1.0]])]});}
            var Q9;
            {var subQ4=sQuery(id+"F0.wireOp",EDGE,"ruCD1RWU-wJnB-kggX-4DZs-hKizQa8h8jOg");Q9=makeQuery(id+"F0.imprint","IMPRINT",FACE,{"disambiguationData":[TD([[makeQuery(id+"F0.imprint","IMPRINT",EDGE,{"derivedFrom":subQ4}),-1.0]])]});}
            var Q10;
            {var subQ5=sQuery(id+"F0.wireOp",EDGE,"A3f7MT6z-twOz-Xzec-rXOm-KRLiCk0BcTYY");Q10=makeQuery(id+"F0.imprint","IMPRINT",FACE,{"disambiguationData":[TD([[makeQuery(id+"F0.imprint","IMPRINT",EDGE,{"derivedFrom":subQ5}),-1.0]])]});}
            var Q11;
            {var subQ9=sQuery(id+"F0.wireOp",EDGE,"E118");Q11=makeQuery(id+"F0.imprint","IMPRINT",FACE,{"disambiguationData":[TD([[makeQuery(id+"F0.imprint","IMPRINT",EDGE,{"derivedFrom":subQ9}),-1.0]])]});}
            var Q12;
            {var subQ0=sQuery(id+"F0.wireOp",EDGE,"E98");Q12=makeQuery(id+"F0.imprint","IMPRINT",FACE,{"disambiguationData":[TD([[makeQuery(id+"F0.imprint","IMPRINT",EDGE,{"derivedFrom":subQ0}),1.0]])]});}
            var Q13;
            {var subQ0=sQuery(id+"F0.wireOp",EDGE,"E119");Q13=makeQuery(id+"F0.imprint","IMPRINT",FACE,{"disambiguationData":[TD([[makeQuery(id+"F0.imprint","IMPRINT",EDGE,{"derivedFrom":subQ0}),-1.0]])]});}
            var Q14;
            {var subQ0=sQuery(id+"F0.wireOp",EDGE,"E143");var subQ1=makeQuery(id+"F0.imprint","IMPRINT",VERTEX,{"derivedFrom":subQ0});Q14=makeQuery(id+"F0.imprint","IMPRINT",FACE,{"disambiguationData":[TD([[makeQuery(id+"F0.imprint","IMPRINT",EDGE,{"disambiguationData":[TD([[subQ1,1.0]])],"derivedFrom":subQ0}),-1.0]])]});}
            var Q15;
            {var subQ0=sQuery(id+"F0.wireOp",EDGE,"E199.MirrorCS");Q15=makeQuery(id+"F0.imprint","IMPRINT",FACE,{"disambiguationData":[TD([[makeQuery(id+"F0.imprint","IMPRINT",EDGE,{"derivedFrom":subQ0}),1.0]])]});}
            var Q16;
            {var subQ7=sQuery(id+"F0.wireOp",EDGE,"E184");Q16=makeQuery(id+"F0.imprint","IMPRINT",FACE,{"disambiguationData":[TD([[makeQuery(id+"F0.imprint","IMPRINT",EDGE,{"derivedFrom":subQ7}),-1.0]])]});}
            extrude(context, id + "F4", {"entities" : qUnion([Q0, Q1, Q2, Q3, Q4, Q5, Q6, Q7, Q8, Q9, Q10, Q11, Q12, Q13, Q14, Q15, Q16]), "operationType" : NewBodyOperationType.REMOVE, "oppositeDirection" : true, "depth" : 30 * mm, "offsetDistance" : 25 * mm, "hasSecondDirection" : true, "secondDirectionOppositeDirection" : true, "secondDirectionDepth" : 8 * mm});
        }
        {
            var Q0;
            {var subQ0=sQuery(id+"F0.wireOp",EDGE,"E26");var subQ1=sQuery(id+"F0.wireOp",EDGE,"E1.bottom");var subQ2=makeQuery(id+"F0.imprint","INTERSECT",VERTEX,{"derivedFrom":[subQ1,subQ0]});Q0=makeQuery(id+"F0.imprint","IMPRINT",FACE,{"disambiguationData":[TD([[makeQuery(id+"F0.imprint","IMPRINT",EDGE,{"disambiguationData":[TD([[subQ2,-1.0]])],"derivedFrom":subQ1}),-1.0]])]});}
            extrude(context, id + "F5", {"entities" : qUnion([Q0]), "operationType" : NewBodyOperationType.ADD, "oppositeDirection" : true, "depth" : 4 * mm, "offsetDistance" : 25 * mm});
        }
        {
            var Q0;
            Q0=makeQuery(id+"F0.imprint","IMPRINT",FACE,{"disambiguationData":[TD([[makeQuery(id+"F0.imprint","IMPRINT",EDGE,{"derivedFrom":sQuery(id+"F0.wireOp",EDGE,"E20")}),-1.0]])]});
            extrude(context, id + "F6", {"entities" : qUnion([Q0]), "operationType" : NewBodyOperationType.ADD, "oppositeDirection" : true, "depth" : 10 * mm, "offsetDistance" : 25 * mm});
        }
        {
            var Q0;
            Q0=makeQuery(id+"F0.imprint","IMPRINT",FACE,{"disambiguationData":[TD([[makeQuery(id+"F0.imprint","IMPRINT",EDGE,{"derivedFrom":sQuery(id+"F0.wireOp",EDGE,"2283af3e-cc0a-49a2-b88e-c8cb0caea344.left")}),1.0]])]});
            var Q1;
            {var subQ2=sQuery(id+"F0.wireOp",EDGE,"E17");Q1=makeQuery(id+"F0.imprint","IMPRINT",FACE,{"disambiguationData":[TD([[makeQuery(id+"F0.imprint","IMPRINT",EDGE,{"derivedFrom":subQ2}),-1.0]])]});}
            var Q2;
            {var subQ0=sQuery(id+"F0.wireOp",EDGE,"E17");Q2=makeQuery(id+"F0.imprint","IMPRINT",FACE,{"disambiguationData":[TD([[makeQuery(id+"F0.imprint","IMPRINT",EDGE,{"derivedFrom":subQ0}),1.0]])]});}
            var Q3;
            {var subQ3=sQuery(id+"F0.wireOp",EDGE,"E19");Q3=makeQuery(id+"F0.imprint","IMPRINT",FACE,{"disambiguationData":[TD([[makeQuery(id+"F0.imprint","IMPRINT",EDGE,{"derivedFrom":subQ3}),1.0]])]});}
            var Q4;
            Q4=makeQuery(id+"F0.imprint","IMPRINT",FACE,{"disambiguationData":[TD([[makeQuery(id+"F0.imprint","IMPRINT",EDGE,{"derivedFrom":sQuery(id+"F0.wireOp",EDGE,"0f421d93-c379-4f7a-809d-829181558ccf")}),-1.0]])]});
            var Q5;
            {var subQ0=sQuery(id+"F0.wireOp",EDGE,"QQ65kaXn-ZlKL-IyBD-f11K-4bzPhy0Ld8Ia");Q5=makeQuery(id+"F0.imprint","IMPRINT",FACE,{"disambiguationData":[TD([[makeQuery(id+"F0.imprint","IMPRINT",EDGE,{"derivedFrom":subQ0}),-1.0]])]});}
            var Q6;
            {var subQ0=sQuery(id+"F0.wireOp",EDGE,"E83");Q6=makeQuery(id+"F0.imprint","IMPRINT",FACE,{"disambiguationData":[TD([[makeQuery(id+"F0.imprint","IMPRINT",EDGE,{"derivedFrom":subQ0}),1.0]])]});}
            var Q7;
            {var subQ2=sQuery(id+"F0.wireOp",EDGE,"E82");Q7=makeQuery(id+"F0.imprint","IMPRINT",FACE,{"disambiguationData":[TD([[makeQuery(id+"F0.imprint","IMPRINT",EDGE,{"derivedFrom":subQ2}),1.0]])]});}
            var Q8;
            {var subQ2=sQuery(id+"F0.wireOp",EDGE,"E84");Q8=makeQuery(id+"F0.imprint","IMPRINT",FACE,{"disambiguationData":[TD([[makeQuery(id+"F0.imprint","IMPRINT",EDGE,{"derivedFrom":subQ2}),1.0]])]});}
            var Q9;
            {var subQ4=sQuery(id+"F0.wireOp",EDGE,"E84");Q9=makeQuery(id+"F0.imprint","IMPRINT",FACE,{"disambiguationData":[TD([[makeQuery(id+"F0.imprint","IMPRINT",EDGE,{"derivedFrom":subQ4}),-1.0]])]});}
            extrude(context, id + "F7", {"entities" : qUnion([Q0, Q1, Q2, Q3, Q4, Q5, Q6, Q7, Q8, Q9]), "oppositeDirection" : true, "depth" : 30 * mm, "offsetDistance" : 25 * mm});
        }
        {
            var Q0;
            {var subQ1=sQuery(id+"F0.wireOp",EDGE,"E17");Q0=makeQuery(id+"F0.imprint","IMPRINT",FACE,{"disambiguationData":[TD([[makeQuery(id+"F0.imprint","IMPRINT",EDGE,{"derivedFrom":subQ1}),1.0]])]});}
            extrude(context, id + "F8", {"entities" : qUnion([Q0]), "operationType" : NewBodyOperationType.REMOVE, "oppositeDirection" : true, "depth" : 10 * mm, "offsetDistance" : 25 * mm});
        }
        {
            var Q0;
            {var subQ0=sQuery(id+"F0.wireOp",EDGE,"E155.MirrorC");var subQ1=sQuery(id+"F0.wireOp",EDGE,"E14.left");var subQ2=makeQuery(id+"F0.imprint","INTERSECT",VERTEX,{"disambiguationData":[OD(0.0)],"derivedFrom":[subQ1,subQ0]});Q0=makeQuery(id+"F0.imprint","IMPRINT",FACE,{"disambiguationData":[TD([[makeQuery(id+"F0.imprint","IMPRINT",EDGE,{"disambiguationData":[TD([[subQ2,-1.0]])],"derivedFrom":subQ1}),-1.0]])]});}
            var Q1;
            {var subQ0=sQuery(id+"F0.wireOp",EDGE,"E155.MirrorC");var subQ1=sQuery(id+"F0.wireOp",EDGE,"E14.left");var subQ2=makeQuery(id+"F0.imprint","INTERSECT",VERTEX,{"disambiguationData":[OD(0.0)],"derivedFrom":[subQ1,subQ0]});Q1=makeQuery(id+"F0.imprint","IMPRINT",FACE,{"disambiguationData":[TD([[makeQuery(id+"F0.imprint","IMPRINT",EDGE,{"disambiguationData":[TD([[subQ2,-1.0]])],"derivedFrom":subQ1}),1.0]])]});}
            var Q2;
            {var subQ0=sQuery(id+"F0.wireOp",EDGE,"E153");var subQ1=sQuery(id+"F0.wireOp",EDGE,"E15.MirrorCS");var subQ2=makeQuery(id+"F0.imprint","INTERSECT",VERTEX,{"disambiguationData":[OD(0.0)],"derivedFrom":[subQ1,subQ0]});Q2=makeQuery(id+"F0.imprint","IMPRINT",FACE,{"disambiguationData":[TD([[makeQuery(id+"F0.imprint","IMPRINT",EDGE,{"disambiguationData":[TD([[subQ2,-1.0]])],"derivedFrom":subQ1}),-1.0]])]});}
            var Q3;
            {var subQ0=sQuery(id+"F0.wireOp",EDGE,"E153");var subQ1=sQuery(id+"F0.wireOp",EDGE,"E15.MirrorCS");var subQ2=makeQuery(id+"F0.imprint","INTERSECT",VERTEX,{"disambiguationData":[OD(0.0)],"derivedFrom":[subQ1,subQ0]});Q3=makeQuery(id+"F0.imprint","IMPRINT",FACE,{"disambiguationData":[TD([[makeQuery(id+"F0.imprint","IMPRINT",EDGE,{"disambiguationData":[TD([[subQ2,-1.0]])],"derivedFrom":subQ1}),1.0]])]});}
            extrude(context, id + "F9", {"entities" : qUnion([Q0, Q1, Q2, Q3]), "operationType" : NewBodyOperationType.REMOVE, "oppositeDirection" : true, "depth" : 30 * mm, "offsetDistance" : 25 * mm, "hasSecondDirection" : true, "secondDirectionOppositeDirection" : true, "secondDirectionDepth" : 15 * mm});
        }
        {
            var Q0;
            Q0=makeQuery(id+"F5.opExtrude","CAP_FACE",FACE,{"disambiguationData":[OSD([sQuery(id+"F0.wireOp",EDGE,"E1.bottom"),sQuery(id+"F0.wireOp",EDGE,"E3.MirrorCS"),sQuery(id+"F0.wireOp",EDGE,"E26"),sQuery(id+"F0.wireOp",EDGE,"E85")])],"isStart":false});
            var sketch = newSketch(context, id + "F10", { "sketchPlane" : qUnion([Q0])});
            skLineSegment(sketch, "E228.bottom", {"start": v(235.76, 27.74) * mm, "end": v(275.26, 27.74) * mm});
            skLineSegment(sketch, "E228.top", {"start": v(235.76, -10.26) * mm, "end": v(275.26, -10.26) * mm});
            skLineSegment(sketch, "E228.left", {"start": v(235.76, 27.74) * mm, "end": v(235.76, -10.26) * mm});
            skLineSegment(sketch, "E228.right", {"start": v(275.26, 27.74) * mm, "end": v(275.26, -10.26) * mm});
            skCircle(sketch, "E229", {"center": v(250.76, 8.74) * mm, "radius": 3 * mm});
            skPoint(sketch, "E229.centerSnap0", {"position": v(255.51, 27.74) * mm});
            skPoint(sketch, "E229.centerSnap1", {"position": v(235.76, 8.74) * mm});
            skCircle(sketch, "E230", {"center": v(250.76, 8.74) * mm, "radius": 13.5 * mm});
            skLineSegment(sketch, "E231", {"start": v(275.26, 8.74) * mm, "end": v(265.73, 8.74) * mm});
            skLineSegment(sketch, "E232.bottom", {"start": v(266.26, 0.24) * mm, "end": v(275.26, 0.24) * mm});
            skLineSegment(sketch, "E232.top", {"start": v(266.26, 17.24) * mm, "end": v(275.26, 17.24) * mm});
            skLineSegment(sketch, "E232.left", {"start": v(266.26, 0.24) * mm, "end": v(266.26, 17.24) * mm});
            skLineSegment(sketch, "E232.right", {"start": v(275.26, 0.24) * mm, "end": v(275.26, 17.24) * mm});
            skSolve(sketch);
        }
        {
            var Q0;
            {var subQ1=sQuery(id+"F10.wireOp",EDGE,"E228.bottom");Q0=makeQuery(id+"F10.imprint","IMPRINT",FACE,{"disambiguationData":[TD([[makeQuery(id+"F10.imprint","IMPRINT",EDGE,{"derivedFrom":subQ1}),-1.0]])]});}
            extrude(context, id + "F11", {"entities" : qUnion([Q0]), "depth" : 15 * mm, "offsetDistance" : 25 * mm});
        }
        {
            var Q0;
            Q0=makeQuery(id+"F10.imprint","IMPRINT",FACE,{"disambiguationData":[TD([[makeQuery(id+"F10.imprint","IMPRINT",EDGE,{"derivedFrom":sQuery(id+"F10.wireOp",EDGE,"E229")}),-1.0]])]});
            extrude(context, id + "F12", {"entities" : qUnion([Q0]), "operationType" : NewBodyOperationType.ADD, "depth" : 5 * mm, "offsetDistance" : 25 * mm});
        }
        {
            var Q0;
            Q0=makeQuery(id+"F5.opExtrude","CAP_FACE",FACE,{"disambiguationData":[OSD([sQuery(id+"F0.wireOp",EDGE,"E1.bottom"),sQuery(id+"F0.wireOp",EDGE,"E3.MirrorCS"),sQuery(id+"F0.wireOp",EDGE,"E26"),sQuery(id+"F0.wireOp",EDGE,"E85")])],"isStart":false});
            var sketch = newSketch(context, id + "F13", { "sketchPlane" : qUnion([Q0])});
            skLineSegment(sketch, "E233.bottom", {"start": v(-79.4, 221.1) * mm, "end": v(35.6, 221.1) * mm});
            skLineSegment(sketch, "E233.right", {"start": v(77.8, 194.1) * mm, "end": v(77.8, 178.6) * mm});
            skLineSegment(sketch, "E234.MirrorCS", {"start": v(-79.4, 96.1) * mm, "end": v(35.6, 96.1) * mm});
            skLineSegment(sketch, "E235.MirrorCS", {"start": v(77.8, 99.1) * mm, "end": v(77.8, 138.6) * mm});
            skLineSegment(sketch, "E236", {"start": v(-94.4, 99.1) * mm, "end": v(-94.4, 218.1) * mm});
            skLineSegment(sketch, "E237.bottom", {"start": v(-110.4, 225.1) * mm, "end": v(80.8, 225.1) * mm});
            skLineSegment(sketch, "E237.top", {"start": v(-110.4, 92.1) * mm, "end": v(80.8, 92.1) * mm});
            skLineSegment(sketch, "E237.left", {"start": v(-110.4, 225.1) * mm, "end": v(-110.4, 92.1) * mm});
            skLineSegment(sketch, "E237.right", {"start": v(80.8, 225.1) * mm, "end": v(80.8, 92.1) * mm});
            skLineSegment(sketch, "E238", {"start": v(77.8, 173.12) * mm, "end": v(77.8, 158.6) * mm});
            skLineSegment(sketch, "E239", {"start": v(38.8, 96.1) * mm, "end": v(38.8, 138.6) * mm});
            skLineSegment(sketch, "E240", {"start": v(35.6, 96.1) * mm, "end": v(35.6, 221.1) * mm});
            skCircle(sketch, "E241", {"center": v(-102.9, 109.1) * mm, "radius": 2 * mm});
            skCircle(sketch, "E242", {"center": v(-102.9, 208.1) * mm, "radius": 2 * mm});
            skPoint(sketch, "E243", {"position": v(38.8, 158.6) * mm});
            skLineSegment(sketch, "E244", {"start": v(38.8, 173.6) * mm, "end": v(77.8, 173.6) * mm});
            skLineSegment(sketch, "E245", {"start": v(38.8, 143.6) * mm, "end": v(77.8, 143.6) * mm});
            skCircle(sketch, "E246", {"center": v(69.3, 188.6) * mm, "radius": 2 * mm});
            skCircle(sketch, "E247.MirrorC", {"center": v(69.3, 128.6) * mm, "radius": 2 * mm});
            skLineSegment(sketch, "E248", {"start": v(38.8, 178.6) * mm, "end": v(77.8, 178.6) * mm});
            skLineSegment(sketch, "E249", {"start": v(38.8, 138.6) * mm, "end": v(77.8, 138.6) * mm});
            skLineSegment(sketch, "E250.MirrorCS", {"start": v(38.8, 194.1) * mm, "end": v(77.8, 194.1) * mm});
            skLineSegment(sketch, "E251.MirrorCS", {"start": v(76.5, 196.1) * mm, "end": v(76.5, 219.1) * mm});
            skLineSegment(sketch, "E252.MirrorCS", {"start": v(52.71, 219.1) * mm, "end": v(76.5, 219.1) * mm});
            skLineSegment(sketch, "E253.MirrorCS", {"start": v(40.8, 196.1) * mm, "end": v(40.8, 219.1) * mm});
            skLineSegment(sketch, "E254", {"start": v(52.71, 219.1) * mm, "end": v(40.8, 219.1) * mm});
            skLineSegment(sketch, "E255", {"start": v(-79.4, 221.1) * mm, "end": v(-91.4, 221.1) * mm});
            skLineSegment(sketch, "E256", {"start": v(-79.4, 96.1) * mm, "end": v(-91.4, 96.1) * mm});
            skLineSegment(sketch, "E257.trimOffspring", {"start": v(40.8, 196.1) * mm, "end": v(76.5, 196.1) * mm});
            skLineSegment(sketch, "E258.trimOffspring", {"start": v(38.8, 143.6) * mm, "end": v(38.8, 173.6) * mm});
            skLineSegment(sketch, "E259.trimOffspring", {"start": v(38.8, 178.6) * mm, "end": v(38.8, 194.1) * mm});
            skPoint(sketch, "E260.orphan", {"position": v(38.8, 221.1) * mm});
            skLineSegment(sketch, "E261.trimOffspring", {"start": v(38.8, 96.1) * mm, "end": v(74.8, 96.1) * mm});
            skLineSegment(sketch, "E262.trimOffspring", {"start": v(77.8, 173.6) * mm, "end": v(77.8, 173.12) * mm});
            skLineSegment(sketch, "E263.trimOffspring", {"start": v(77.8, 143.6) * mm, "end": v(77.8, 158.6) * mm});
            skPoint(sketch, "E264.visualSharp", {"position": v(77.8, 96.1) * mm});
            skArc(sketch, "E264.filletArc", {"start": v(74.8, 96.1) * mm, "mid": v(76.92, 96.97) * mm, "end": v(77.8, 99.1) * mm});
            skPoint(sketch, "E265.visualSharp", {"position": v(-94.4, 96.1) * mm});
            skArc(sketch, "E265.filletArc", {"start": v(-94.4, 99.1) * mm, "mid": v(-93.52, 96.97) * mm, "end": v(-91.4, 96.1) * mm});
            skPoint(sketch, "E266.visualSharp", {"position": v(-94.4, 221.1) * mm});
            skArc(sketch, "E266.filletArc", {"start": v(-91.4, 221.1) * mm, "mid": v(-93.52, 220.21) * mm, "end": v(-94.4, 218.1) * mm});
            skSolve(sketch);
        }
        {
            var Q0;
            {var subQ0=sQuery(id+"F13.wireOp",EDGE,"E236");Q0=makeQuery(id+"F13.imprint","IMPRINT",FACE,{"disambiguationData":[TD([[makeQuery(id+"F13.imprint","IMPRINT",EDGE,{"derivedFrom":subQ0}),-1.0]])]});}
            var Q1;
            Q1=makeQuery(id+"F13.imprint","IMPRINT",FACE,{"disambiguationData":[TD([[makeQuery(id+"F13.imprint","IMPRINT",EDGE,{"derivedFrom":sQuery(id+"F13.wireOp",EDGE,"E246")}),-1.0]])]});
            var Q2;
            Q2=makeQuery(id+"F13.imprint","IMPRINT",FACE,{"disambiguationData":[TD([[makeQuery(id+"F13.imprint","IMPRINT",EDGE,{"derivedFrom":sQuery(id+"F13.wireOp",EDGE,"E247.MirrorC")}),1.0]])]});
            var Q3;
            {var subQ0=sQuery(id+"F13.wireOp",EDGE,"1WD1SKse-G4Rd-lKen-yjGB-D8RZnCP2YEgS");Q3=makeQuery(id+"F13.imprint","IMPRINT",FACE,{"disambiguationData":[TD([[makeQuery(id+"F13.imprint","IMPRINT",EDGE,{"derivedFrom":subQ0}),-1.0]])]});}
            var Q4;
            {var subQ3=sQuery(id+"F13.wireOp",EDGE,"mBIyQeHb-XQte-vq2O-33cq-PteMLacY3uDZ");Q4=makeQuery(id+"F13.imprint","IMPRINT",FACE,{"disambiguationData":[TD([[makeQuery(id+"F13.imprint","IMPRINT",EDGE,{"derivedFrom":subQ3}),-1.0]])]});}
            var Q5;
            {var subQ0=sQuery(id+"F13.wireOp",EDGE,"mBIyQeHb-XQte-vq2O-33cq-PteMLacY3uDZ");Q5=makeQuery(id+"F13.imprint","IMPRINT",FACE,{"disambiguationData":[TD([[makeQuery(id+"F13.imprint","IMPRINT",EDGE,{"derivedFrom":subQ0}),1.0]])]});}
            var Q6;
            {var subQ5=sQuery(id+"F13.wireOp",EDGE,"FmkZTscd-2qlG-au4n-VbeZ-khHhw21Iq122");Q6=makeQuery(id+"F13.imprint","IMPRINT",FACE,{"disambiguationData":[TD([[makeQuery(id+"F13.imprint","IMPRINT",EDGE,{"derivedFrom":subQ5}),1.0]])]});}
            extrude(context, id + "F14", {"entities" : qUnion([Q0, Q1, Q2, Q3, Q4, Q5, Q6]), "depth" : 5 * mm, "offsetDistance" : 25 * mm});
        }
        {
            var Q0;
            {var subQ10=sQuery(id+"F13.wireOp",EDGE,"E233.right");Q0=makeQuery(id+"F13.imprint","IMPRINT",FACE,{"disambiguationData":[TD([[makeQuery(id+"F13.imprint","IMPRINT",EDGE,{"derivedFrom":subQ10}),1.0]])]});}
            var Q1;
            {var subQ0=sQuery(id+"F13.wireOp",EDGE,"E239");Q1=makeQuery(id+"F13.imprint","IMPRINT",FACE,{"disambiguationData":[TD([[makeQuery(id+"F13.imprint","IMPRINT",EDGE,{"derivedFrom":subQ0}),1.0]])]});}
            var Q2;
            {var subQ0=sQuery(id+"F13.wireOp",EDGE,"E245");Q2=makeQuery(id+"F13.imprint","IMPRINT",FACE,{"disambiguationData":[TD([[makeQuery(id+"F13.imprint","IMPRINT",EDGE,{"derivedFrom":subQ0}),-1.0]])]});}
            var Q3;
            {var subQ0=sQuery(id+"F13.wireOp",EDGE,"E244");Q3=makeQuery(id+"F13.imprint","IMPRINT",FACE,{"disambiguationData":[TD([[makeQuery(id+"F13.imprint","IMPRINT",EDGE,{"derivedFrom":subQ0}),1.0]])]});}
            var Q4;
            {var subQ4=sQuery(id+"F13.wireOp",EDGE,"1WD1SKse-G4Rd-lKen-yjGB-D8RZnCP2YEgS");Q4=makeQuery(id+"F13.imprint","IMPRINT",FACE,{"disambiguationData":[TD([[makeQuery(id+"F13.imprint","IMPRINT",EDGE,{"derivedFrom":subQ4}),-1.0]])]});}
            var Q5;
            {var subQ5=sQuery(id+"F13.wireOp",EDGE,"FmkZTscd-2qlG-au4n-VbeZ-khHhw21Iq122");Q5=makeQuery(id+"F13.imprint","IMPRINT",FACE,{"disambiguationData":[TD([[makeQuery(id+"F13.imprint","IMPRINT",EDGE,{"derivedFrom":subQ5}),1.0]])]});}
            var Q6;
            {var subQ5=sQuery(id+"F13.wireOp",EDGE,"mBIyQeHb-XQte-vq2O-33cq-PteMLacY3uDZ");Q6=makeQuery(id+"F13.imprint","IMPRINT",FACE,{"disambiguationData":[TD([[makeQuery(id+"F13.imprint","IMPRINT",EDGE,{"derivedFrom":subQ5}),-1.0]])]});}
            var Q7;
            {var subQ0=sQuery(id+"F13.wireOp",EDGE,"mBIyQeHb-XQte-vq2O-33cq-PteMLacY3uDZ");Q7=makeQuery(id+"F13.imprint","IMPRINT",FACE,{"disambiguationData":[TD([[makeQuery(id+"F13.imprint","IMPRINT",EDGE,{"derivedFrom":subQ0}),1.0]])]});}
            var Q8;
            {var subQ10=sQuery(id+"F13.wireOp",EDGE,"E253.MirrorCS");Q8=makeQuery(id+"F13.imprint","IMPRINT",FACE,{"disambiguationData":[TD([[makeQuery(id+"F13.imprint","IMPRINT",EDGE,{"derivedFrom":subQ10}),1.0]])]});}
            var Q9;
            {var subQ5=sQuery(id+"F13.wireOp",EDGE,"E251.MirrorCS");Q9=makeQuery(id+"F13.imprint","IMPRINT",FACE,{"disambiguationData":[TD([[makeQuery(id+"F13.imprint","IMPRINT",EDGE,{"derivedFrom":subQ5}),-1.0]])]});}
            var Q10;
            {var subQ5=sQuery(id+"F13.wireOp",EDGE,"E250.MirrorCS");Q10=makeQuery(id+"F13.imprint","IMPRINT",FACE,{"disambiguationData":[TD([[makeQuery(id+"F13.imprint","IMPRINT",EDGE,{"derivedFrom":subQ5}),1.0]])]});}
            var Q11;
            {var subQ0=sQuery(id+"F13.wireOp",EDGE,"eN6ecfd3-31fC-ThTR-l0mG-JTVyOerkcSOT");Q11=makeQuery(id+"F13.imprint","IMPRINT",FACE,{"disambiguationData":[TD([[makeQuery(id+"F13.imprint","IMPRINT",EDGE,{"derivedFrom":subQ0}),-1.0]])]});}
            extrude(context, id + "F15", {"entities" : qUnion([Q0, Q1, Q2, Q3, Q4, Q5, Q6, Q7, Q8, Q9, Q10, Q11]), "depth" : 2 * mm, "offsetDistance" : 25 * mm});
        }
        {
            var Q0;
            Q0=makeQuery(id+"F5.opExtrude","CAP_FACE",FACE,{"disambiguationData":[OSD([sQuery(id+"F0.wireOp",EDGE,"E1.bottom"),sQuery(id+"F0.wireOp",EDGE,"E3.MirrorCS"),sQuery(id+"F0.wireOp",EDGE,"E26"),sQuery(id+"F0.wireOp",EDGE,"E85")])],"isStart":false});
            var sketch = newSketch(context, id + "F16", { "sketchPlane" : qUnion([Q0])});
            skLineSegment(sketch, "E267.MirrorCS", {"start": v(157.36, 66.81) * mm, "end": v(166.36, 66.81) * mm});
            skLineSegment(sketch, "E268.MirrorCS", {"start": v(154.36, 57.81) * mm, "end": v(154.36, 61.81) * mm});
            skLineSegment(sketch, "E269.MirrorCS", {"start": v(169.16, 57.81) * mm, "end": v(169.16, 61.81) * mm});
            skLineSegment(sketch, "E270", {"start": v(157.36, 54.81) * mm, "end": v(166.16, 54.81) * mm});
            skLineSegment(sketch, "E271", {"start": v(157.36, 64.81) * mm, "end": v(166.16, 64.81) * mm});
            skLineSegment(sketch, "E272", {"start": v(157.36, 52.81) * mm, "end": v(166.16, 52.81) * mm});
            skLineSegment(sketch, "E273", {"start": v(155.88, 41.31) * mm, "end": v(162.88, 41.31) * mm});
            skArc(sketch, "E274.filletArc", {"start": v(157.36, 66.81) * mm, "mid": v(155.24, 65.93) * mm, "end": v(154.36, 63.81) * mm});
            skLineSegment(sketch, "E275", {"start": v(154.36, 41.31) * mm, "end": v(154.36, 44.31) * mm});
            skCircle(sketch, "E276", {"center": v(169.66, 24.28) * mm, "radius": 2.55 * mm});
            skCircle(sketch, "E277.MirrorC", {"center": v(161.86, 47.31) * mm, "radius": 2.55 * mm});
            skArc(sketch, "E278.filletArc", {"start": v(154.36, 57.81) * mm, "mid": v(155.24, 55.69) * mm, "end": v(157.36, 54.81) * mm});
            skArc(sketch, "E279.filletArc", {"start": v(166.16, 54.81) * mm, "mid": v(168.28, 55.69) * mm, "end": v(169.16, 57.81) * mm});
            skLineSegment(sketch, "E280", {"start": v(154.36, 57.81) * mm, "end": v(154.36, 55.81) * mm});
            skLineSegment(sketch, "E281", {"start": v(169.16, 57.81) * mm, "end": v(169.16, 55.81) * mm});
            skArc(sketch, "E282.filletArc", {"start": v(154.36, 55.81) * mm, "mid": v(155.24, 53.69) * mm, "end": v(157.36, 52.81) * mm});
            skArc(sketch, "E283.filletArc", {"start": v(166.16, 52.81) * mm, "mid": v(168.28, 53.69) * mm, "end": v(169.16, 55.81) * mm});
            skLineSegment(sketch, "E284", {"start": v(154.36, 55.81) * mm, "end": v(154.36, 45.81) * mm});
            skArc(sketch, "E285.filletArc", {"start": v(157.36, 64.81) * mm, "mid": v(155.24, 63.93) * mm, "end": v(154.36, 61.81) * mm});
            skArc(sketch, "E286.filletArc", {"start": v(169.16, 61.81) * mm, "mid": v(168.28, 63.93) * mm, "end": v(166.16, 64.81) * mm});
            skLineSegment(sketch, "E287", {"start": v(154.36, 61.81) * mm, "end": v(154.36, 63.81) * mm});
            skArc(sketch, "E288.filletArc", {"start": v(174.16, 16.63) * mm, "mid": v(176.28, 17.51) * mm, "end": v(177.16, 19.63) * mm});
            skLineSegment(sketch, "E289", {"start": v(155.88, 41.31) * mm, "end": v(154.36, 41.31) * mm});
            skLineSegment(sketch, "E290", {"start": v(162.88, 41.31) * mm, "end": v(169.16, 41.31) * mm});
            skLineSegment(sketch, "E291", {"start": v(154.36, 41.31) * mm, "end": v(169.16, 41.31) * mm});
            skLineSegment(sketch, "E292", {"start": v(154.36, 45.81) * mm, "end": v(154.36, 44.31) * mm});
            skLineSegment(sketch, "E293.MirrorCS", {"start": v(181.16, 60.3) * mm, "end": v(181.16, 63.8) * mm});
            skLineSegment(sketch, "E294.MirrorCS", {"start": v(166.16, 66.81) * mm, "end": v(166.16, 66.81) * mm});
            skLineSegment(sketch, "E295", {"start": v(169.16, 61.81) * mm, "end": v(169.16, 63.81) * mm});
            skPoint(sketch, "E296.newPointB", {"position": v(181.16, 66.8) * mm});
            skArc(sketch, "E296.filletArc", {"start": v(169.16, 63.81) * mm, "mid": v(168.28, 65.93) * mm, "end": v(166.16, 66.81) * mm});
            skLineSegment(sketch, "E297", {"start": v(166.16, 66.81) * mm, "end": v(181.16, 66.8) * mm});
            skLineSegment(sketch, "E298", {"start": v(157.36, 29.88) * mm, "end": v(157.36, 16.63) * mm});
            skCircle(sketch, "E299.MirrorC", {"center": v(161.26, 2.59) * mm, "radius": 2.55 * mm});
            skLineSegment(sketch, "E300.MirrorCS", {"start": v(153.76, 1.62) * mm, "end": v(153.76, -0.41) * mm});
            skLineSegment(sketch, "E301.MirrorCS", {"start": v(168.56, -0.41) * mm, "end": v(168.56, 5.62) * mm});
            skLineSegment(sketch, "E302", {"start": v(148.57, 8.62) * mm, "end": v(153.76, 8.62) * mm});
            skLineSegment(sketch, "E303", {"start": v(148.57, 1.62) * mm, "end": v(153.76, 1.62) * mm});
            skLineSegment(sketch, "E304", {"start": v(168.56, -0.41) * mm, "end": v(168.56, -11.91) * mm});
            skLineSegment(sketch, "E305", {"start": v(151.57, 8.62) * mm, "end": v(148.57, 8.62) * mm});
            skLineSegment(sketch, "E306", {"start": v(153.76, 8.62) * mm, "end": v(165.56, 8.62) * mm});
            skArc(sketch, "E307.filletArc", {"start": v(168.56, 5.62) * mm, "mid": v(167.69, 7.74) * mm, "end": v(165.56, 8.62) * mm});
            skLineSegment(sketch, "E308", {"start": v(168.76, -16.41) * mm, "end": v(180.76, -16.4) * mm});
            skLineSegment(sketch, "E309", {"start": v(180.76, -16.4) * mm, "end": v(180.76, -19.9) * mm});
            skPoint(sketch, "E310.newPointA", {"position": v(180.76, -22.9) * mm});
            skLineSegment(sketch, "E311", {"start": v(165.76, -22.91) * mm, "end": v(180.76, -22.9) * mm});
            skLineSegment(sketch, "E312", {"start": v(153.77, -11.91) * mm, "end": v(153.76, -0.41) * mm});
            skLineSegment(sketch, "E313.MirrorCS", {"start": v(165.56, -22.91) * mm, "end": v(165.57, -22.91) * mm});
            skLineSegment(sketch, "E314.MirrorCS", {"start": v(168.56, -13.91) * mm, "end": v(168.56, -11.91) * mm});
            skLineSegment(sketch, "E315.MirrorCS", {"start": v(153.76, -17.91) * mm, "end": v(153.76, -19.91) * mm});
            skLineSegment(sketch, "E316.MirrorCS", {"start": v(156.76, -8.91) * mm, "end": v(165.76, -8.91) * mm});
            skLineSegment(sketch, "E317.MirrorCS", {"start": v(156.76, -20.91) * mm, "end": v(165.76, -20.91) * mm});
            skLineSegment(sketch, "E318.MirrorCS", {"start": v(156.76, -22.91) * mm, "end": v(165.76, -22.91) * mm});
            skArc(sketch, "E319.MirrorCS", {"start": v(156.76, -20.91) * mm, "mid": v(154.64, -20.03) * mm, "end": v(153.76, -17.91) * mm});
            skArc(sketch, "E320.MirrorCS", {"start": v(165.76, -10.91) * mm, "mid": v(167.76, -11.86) * mm, "end": v(168.56, -13.91) * mm});
            skLineSegment(sketch, "E321.MirrorCS", {"start": v(153.76, -13.91) * mm, "end": v(153.76, -11.91) * mm});
            skLineSegment(sketch, "E322.MirrorCS", {"start": v(168.56, -17.91) * mm, "end": v(168.56, -19.91) * mm});
            skArc(sketch, "E323.MirrorCS", {"start": v(156.76, -22.91) * mm, "mid": v(154.64, -22.03) * mm, "end": v(153.76, -19.91) * mm});
            skArc(sketch, "E324.MirrorCS", {"start": v(153.76, -13.91) * mm, "mid": v(154.64, -11.79) * mm, "end": v(156.76, -10.91) * mm});
            skArc(sketch, "E325.MirrorCS", {"start": v(153.76, -11.91) * mm, "mid": v(154.64, -9.79) * mm, "end": v(156.76, -8.91) * mm});
            skLineSegment(sketch, "E326.MirrorCS", {"start": v(153.76, -13.91) * mm, "end": v(153.76, -17.91) * mm});
            skLineSegment(sketch, "E327.MirrorCS", {"start": v(156.76, -10.91) * mm, "end": v(165.76, -10.91) * mm});
            skLineSegment(sketch, "E328.MirrorCS", {"start": v(168.56, -13.91) * mm, "end": v(168.56, -17.91) * mm});
            skArc(sketch, "E329.MirrorCS", {"start": v(168.56, -19.91) * mm, "mid": v(167.69, -22.03) * mm, "end": v(165.57, -22.91) * mm});
            skArc(sketch, "E330.MirrorCS", {"start": v(165.76, -8.91) * mm, "mid": v(167.76, -9.86) * mm, "end": v(168.56, -11.91) * mm});
            skArc(sketch, "E331.MirrorCS", {"start": v(168.56, -17.91) * mm, "mid": v(167.76, -19.96) * mm, "end": v(165.76, -20.91) * mm});
            skLineSegment(sketch, "E332", {"start": v(148.57, 8.62) * mm, "end": v(148.57, 1.62) * mm});
            skLineSegment(sketch, "E333.MirrorCS", {"start": v(180.76, 50.28) * mm, "end": v(189.76, 50.28) * mm});
            skLineSegment(sketch, "E334.MirrorCS", {"start": v(177.76, 41.28) * mm, "end": v(177.76, 45.28) * mm});
            skLineSegment(sketch, "E335.MirrorCS", {"start": v(192.56, 41.28) * mm, "end": v(192.56, 45.28) * mm});
            skLineSegment(sketch, "E336", {"start": v(180.76, 38.28) * mm, "end": v(189.56, 38.28) * mm});
            skLineSegment(sketch, "E337", {"start": v(180.76, 48.28) * mm, "end": v(189.56, 48.28) * mm});
            skLineSegment(sketch, "E338", {"start": v(180.76, 36.28) * mm, "end": v(189.56, 36.28) * mm});
            skArc(sketch, "E339.filletArc", {"start": v(180.76, 50.28) * mm, "mid": v(178.64, 49.4) * mm, "end": v(177.76, 47.28) * mm});
            skArc(sketch, "E340.filletArc", {"start": v(177.76, 41.28) * mm, "mid": v(178.64, 39.16) * mm, "end": v(180.76, 38.28) * mm});
            skArc(sketch, "E341.filletArc", {"start": v(189.56, 38.28) * mm, "mid": v(191.69, 39.16) * mm, "end": v(192.56, 41.28) * mm});
            skLineSegment(sketch, "E342", {"start": v(177.76, 41.28) * mm, "end": v(177.76, 39.28) * mm});
            skLineSegment(sketch, "E343", {"start": v(192.56, 41.28) * mm, "end": v(192.56, 39.28) * mm});
            skArc(sketch, "E344.filletArc", {"start": v(177.76, 39.28) * mm, "mid": v(178.64, 37.16) * mm, "end": v(180.76, 36.28) * mm});
            skArc(sketch, "E345.filletArc", {"start": v(189.56, 36.28) * mm, "mid": v(191.69, 37.16) * mm, "end": v(192.56, 39.28) * mm});
            skArc(sketch, "E346.filletArc", {"start": v(180.76, 48.28) * mm, "mid": v(178.64, 47.4) * mm, "end": v(177.76, 45.28) * mm});
            skArc(sketch, "E347.filletArc", {"start": v(192.56, 45.28) * mm, "mid": v(191.69, 47.4) * mm, "end": v(189.56, 48.28) * mm});
            skLineSegment(sketch, "E348", {"start": v(177.76, 45.28) * mm, "end": v(177.76, 47.28) * mm});
            skLineSegment(sketch, "E349.MirrorCS", {"start": v(189.56, 50.28) * mm, "end": v(189.57, 50.28) * mm});
            skLineSegment(sketch, "E350", {"start": v(192.56, 45.28) * mm, "end": v(192.56, 47.28) * mm});
            skArc(sketch, "E351.filletArc", {"start": v(192.56, 47.28) * mm, "mid": v(191.69, 49.4) * mm, "end": v(189.57, 50.28) * mm});
            skLineSegment(sketch, "E352.MirrorCS", {"start": v(189.2, -6.53) * mm, "end": v(189.2, -6.53) * mm});
            skLineSegment(sketch, "E353.MirrorCS", {"start": v(192.2, 2.47) * mm, "end": v(192.2, 4.47) * mm});
            skLineSegment(sketch, "E354.MirrorCS", {"start": v(177.4, -1.53) * mm, "end": v(177.4, -3.53) * mm});
            skLineSegment(sketch, "E355.MirrorCS", {"start": v(180.4, 7.47) * mm, "end": v(189.4, 7.47) * mm});
            skLineSegment(sketch, "E356.MirrorCS", {"start": v(180.4, -4.53) * mm, "end": v(189.4, -4.53) * mm});
            skLineSegment(sketch, "E357.MirrorCS", {"start": v(180.4, -6.53) * mm, "end": v(189.4, -6.53) * mm});
            skArc(sketch, "E358.MirrorCS", {"start": v(180.4, -4.53) * mm, "mid": v(178.28, -3.65) * mm, "end": v(177.4, -1.53) * mm});
            skArc(sketch, "E359.MirrorCS", {"start": v(189.4, 5.47) * mm, "mid": v(191.39, 4.53) * mm, "end": v(192.2, 2.47) * mm});
            skLineSegment(sketch, "E360.MirrorCS", {"start": v(177.4, 2.47) * mm, "end": v(177.4, 4.47) * mm});
            skLineSegment(sketch, "E361.MirrorCS", {"start": v(192.2, -1.53) * mm, "end": v(192.2, -3.53) * mm});
            skArc(sketch, "E362.MirrorCS", {"start": v(180.4, -6.53) * mm, "mid": v(178.28, -5.65) * mm, "end": v(177.4, -3.53) * mm});
            skArc(sketch, "E363.MirrorCS", {"start": v(177.4, 2.47) * mm, "mid": v(178.28, 4.6) * mm, "end": v(180.4, 5.47) * mm});
            skArc(sketch, "E364.MirrorCS", {"start": v(177.4, 4.47) * mm, "mid": v(178.28, 6.6) * mm, "end": v(180.4, 7.47) * mm});
            skLineSegment(sketch, "E365.MirrorCS", {"start": v(177.4, 2.47) * mm, "end": v(177.4, -1.53) * mm});
            skLineSegment(sketch, "E366.MirrorCS", {"start": v(180.4, 5.47) * mm, "end": v(189.4, 5.47) * mm});
            skLineSegment(sketch, "E367.MirrorCS", {"start": v(192.2, 2.47) * mm, "end": v(192.2, -1.53) * mm});
            skArc(sketch, "E368.MirrorCS", {"start": v(192.2, -3.53) * mm, "mid": v(191.32, -5.65) * mm, "end": v(189.2, -6.53) * mm});
            skArc(sketch, "E369.MirrorCS", {"start": v(189.4, 7.47) * mm, "mid": v(191.39, 6.53) * mm, "end": v(192.2, 4.47) * mm});
            skArc(sketch, "E370.MirrorCS", {"start": v(192.2, -1.53) * mm, "mid": v(191.39, -3.58) * mm, "end": v(189.4, -4.53) * mm});
            skLineSegment(sketch, "E371", {"start": v(168.76, -16.41) * mm, "end": v(168.56, -16.41) * mm});
            skLineSegment(sketch, "E372", {"start": v(180.76, -22.9) * mm, "end": v(190.76, -22.9) * mm});
            skLineSegment(sketch, "E373", {"start": v(190.76, -22.9) * mm, "end": v(190.76, -19.9) * mm});
            skLineSegment(sketch, "E374", {"start": v(180.76, -19.9) * mm, "end": v(190.76, -19.9) * mm});
            skLineSegment(sketch, "E375", {"start": v(181.16, 66.8) * mm, "end": v(191.16, 66.8) * mm});
            skLineSegment(sketch, "E376", {"start": v(191.16, 63.8) * mm, "end": v(191.16, 66.8) * mm});
            skLineSegment(sketch, "E377", {"start": v(191.16, 63.8) * mm, "end": v(181.16, 63.8) * mm});
            skLineSegment(sketch, "E378", {"start": v(177.16, 29.88) * mm, "end": v(157.36, 29.88) * mm});
            skLineSegment(sketch, "E379", {"start": v(174.16, 16.63) * mm, "end": v(157.36, 16.63) * mm});
            skLineSegment(sketch, "E380", {"start": v(177.16, 29.88) * mm, "end": v(177.16, 19.63) * mm});
            skLineSegment(sketch, "E381", {"start": v(181.16, 60.3) * mm, "end": v(169.16, 60.3) * mm});
            skLineSegment(sketch, "E382", {"start": v(169.16, 60.3) * mm, "end": v(169.16, 55.81) * mm});
            skLineSegment(sketch, "E383", {"start": v(169.16, 41.31) * mm, "end": v(169.16, 60.3) * mm});
            skSolve(sketch);
        }
        {
            var Q0;
            Q0=makeQuery(id+"F16.imprint","IMPRINT",FACE,{"disambiguationData":[TD([[makeQuery(id+"F16.imprint","IMPRINT",EDGE,{"derivedFrom":sQuery(id+"F16.wireOp",EDGE,"e648a1b0-139c-4d00-941e-85c32a210807")}),1.0]])]});
            var Q1;
            {var subQ0=sQuery(id+"F16.wireOp",EDGE,"E372");Q1=makeQuery(id+"F16.imprint","IMPRINT",FACE,{"disambiguationData":[TD([[makeQuery(id+"F16.imprint","IMPRINT",EDGE,{"derivedFrom":subQ0}),1.0]])]});}
            var Q2;
            Q2=makeQuery(id+"F16.imprint","IMPRINT",FACE,{"disambiguationData":[TD([[makeQuery(id+"F16.imprint","IMPRINT",EDGE,{"derivedFrom":sQuery(id+"F16.wireOp",EDGE,"E337")}),1.0]])]});
            var Q3;
            Q3=makeQuery(id+"F16.imprint","IMPRINT",FACE,{"disambiguationData":[TD([[makeQuery(id+"F16.imprint","IMPRINT",EDGE,{"derivedFrom":sQuery(id+"F16.wireOp",EDGE,"E336")}),-1.0]])]});
            var Q4;
            {var subQ1=sQuery(id+"F16.wireOp",EDGE,"E353.MirrorCS");Q4=makeQuery(id+"F16.imprint","IMPRINT",FACE,{"disambiguationData":[TD([[makeQuery(id+"F16.imprint","IMPRINT",EDGE,{"derivedFrom":subQ1}),1.0]])]});}
            var Q5;
            Q5=makeQuery(id+"F16.imprint","IMPRINT",FACE,{"disambiguationData":[TD([[makeQuery(id+"F16.imprint","IMPRINT",EDGE,{"derivedFrom":sQuery(id+"F16.wireOp",EDGE,"E354.MirrorCS")}),1.0]])]});
            var Q6;
            {var subQ0=sQuery(id+"F16.wireOp",EDGE,"E297");var subQ1=sQuery(id+"F16.wireOp",EDGE,"E267.MirrorCS");var subQ2=makeQuery(id+"F16.imprint","INTERSECT",VERTEX,{"derivedFrom":[subQ1,subQ0]});Q6=makeQuery(id+"F16.imprint","IMPRINT",FACE,{"disambiguationData":[TD([[makeQuery(id+"F16.imprint","IMPRINT",EDGE,{"disambiguationData":[TD([[subQ2,1.0]])],"derivedFrom":subQ0}),1.0]])]});}
            var Q7;
            Q7=makeQuery(id+"F16.imprint","IMPRINT",FACE,{"disambiguationData":[TD([[makeQuery(id+"F16.imprint","IMPRINT",EDGE,{"derivedFrom":sQuery(id+"F16.wireOp",EDGE,"E270")}),-1.0]])]});
            var Q8;
            Q8=makeQuery(id+"F16.imprint","IMPRINT",FACE,{"disambiguationData":[TD([[makeQuery(id+"F16.imprint","IMPRINT",EDGE,{"derivedFrom":sQuery(id+"F16.wireOp",EDGE,"E272")}),-1.0]])]});
            var Q9;
            Q9=makeQuery(id+"F16.imprint","IMPRINT",FACE,{"disambiguationData":[TD([[makeQuery(id+"F16.imprint","IMPRINT",EDGE,{"derivedFrom":sQuery(id+"F16.wireOp",EDGE,"E299.MirrorC")}),1.0]])]});
            var Q10;
            {var subQ8=sQuery(id+"F16.wireOp",EDGE,"E314.MirrorCS");Q10=makeQuery(id+"F16.imprint","IMPRINT",FACE,{"disambiguationData":[TD([[makeQuery(id+"F16.imprint","IMPRINT",EDGE,{"derivedFrom":subQ8}),1.0]])]});}
            var Q11;
            Q11=makeQuery(id+"F16.imprint","IMPRINT",FACE,{"disambiguationData":[TD([[makeQuery(id+"F16.imprint","IMPRINT",EDGE,{"derivedFrom":sQuery(id+"F16.wireOp",EDGE,"E315.MirrorCS")}),1.0]])]});
            var Q12;
            Q12=makeQuery(id+"F16.imprint","IMPRINT",FACE,{"disambiguationData":[TD([[makeQuery(id+"F16.imprint","IMPRINT",EDGE,{"derivedFrom":sQuery(id+"F16.wireOp",EDGE,"E334.MirrorCS")}),-1.0]])]});
            var Q13;
            {var subQ6=sQuery(id+"F16.wireOp",EDGE,"E356.MirrorCS");Q13=makeQuery(id+"F16.imprint","IMPRINT",FACE,{"disambiguationData":[TD([[makeQuery(id+"F16.imprint","IMPRINT",EDGE,{"derivedFrom":subQ6}),1.0]])]});}
            var Q14;
            {var subQ8=sQuery(id+"F16.wireOp",EDGE,"E308");Q14=makeQuery(id+"F16.imprint","IMPRINT",FACE,{"disambiguationData":[TD([[makeQuery(id+"F16.imprint","IMPRINT",EDGE,{"derivedFrom":subQ8}),-1.0]])]});}
            var Q15;
            {var subQ5=sQuery(id+"F16.wireOp",EDGE,"E317.MirrorCS");Q15=makeQuery(id+"F16.imprint","IMPRINT",FACE,{"disambiguationData":[TD([[makeQuery(id+"F16.imprint","IMPRINT",EDGE,{"derivedFrom":subQ5}),1.0]])]});}
            var Q16;
            {var subQ0=sQuery(id+"F16.wireOp",EDGE,"E375");Q16=makeQuery(id+"F16.imprint","IMPRINT",FACE,{"disambiguationData":[TD([[makeQuery(id+"F16.imprint","IMPRINT",EDGE,{"derivedFrom":subQ0}),-1.0]])]});}
            var Q17;
            {var subQ6=sQuery(id+"F16.wireOp",EDGE,"E295");Q17=makeQuery(id+"F16.imprint","IMPRINT",FACE,{"disambiguationData":[TD([[makeQuery(id+"F16.imprint","IMPRINT",EDGE,{"derivedFrom":subQ6}),-1.0]])]});}
            var Q18;
            Q18=makeQuery(id+"F16.imprint","IMPRINT",FACE,{"disambiguationData":[TD([[makeQuery(id+"F16.imprint","IMPRINT",EDGE,{"derivedFrom":sQuery(id+"F16.wireOp",EDGE,"E276")}),-1.0]])]});
            extrude(context, id + "F17", {"entities" : qUnion([Q0, Q1, Q2, Q3, Q4, Q5, Q6, Q7, Q8, Q9, Q10, Q11, Q12, Q13, Q14, Q15, Q16, Q17, Q18]), "depth" : 5 * mm, "offsetDistance" : 25 * mm});
        }
        {
            var Q0;
            Q0=makeQuery(id+"F16.imprint","IMPRINT",FACE,{"disambiguationData":[TD([[makeQuery(id+"F16.imprint","IMPRINT",EDGE,{"derivedFrom":sQuery(id+"F16.wireOp",EDGE,"E270")}),-1.0]])]});
            var Q1;
            Q1=makeQuery(id+"F16.imprint","IMPRINT",FACE,{"disambiguationData":[TD([[makeQuery(id+"F16.imprint","IMPRINT",EDGE,{"derivedFrom":sQuery(id+"F16.wireOp",EDGE,"E268.MirrorCS")}),-1.0]])]});
            var Q2;
            {var subQ6=sQuery(id+"F16.wireOp",EDGE,"E356.MirrorCS");Q2=makeQuery(id+"F16.imprint","IMPRINT",FACE,{"disambiguationData":[TD([[makeQuery(id+"F16.imprint","IMPRINT",EDGE,{"derivedFrom":subQ6}),1.0]])]});}
            var Q3;
            Q3=makeQuery(id+"F16.imprint","IMPRINT",FACE,{"disambiguationData":[TD([[makeQuery(id+"F16.imprint","IMPRINT",EDGE,{"derivedFrom":sQuery(id+"F16.wireOp",EDGE,"E334.MirrorCS")}),-1.0]])]});
            var Q4;
            Q4=makeQuery(id+"F16.imprint","IMPRINT",FACE,{"disambiguationData":[TD([[makeQuery(id+"F16.imprint","IMPRINT",EDGE,{"derivedFrom":sQuery(id+"F16.wireOp",EDGE,"E271")}),1.0]])]});
            extrude(context, id + "F18", {"entities" : qUnion([Q0, Q1, Q2, Q3, Q4]), "operationType" : NewBodyOperationType.ADD, "depth" : 10 * mm, "offsetDistance" : 25 * mm});
        }
        {
            var Q0;
            {var subQ4=sQuery(id+"F16.wireOp",EDGE,"E317.MirrorCS");Q0=makeQuery(id+"F16.imprint","IMPRINT",FACE,{"disambiguationData":[TD([[makeQuery(id+"F16.imprint","IMPRINT",EDGE,{"derivedFrom":subQ4}),1.0]])]});}
            var Q1;
            {var subQ6=sQuery(id+"F16.wireOp",EDGE,"E314.MirrorCS");Q1=makeQuery(id+"F16.imprint","IMPRINT",FACE,{"disambiguationData":[TD([[makeQuery(id+"F16.imprint","IMPRINT",EDGE,{"derivedFrom":subQ6}),1.0]])]});}
            var Q2;
            Q2=makeQuery(id+"F16.imprint","IMPRINT",FACE,{"disambiguationData":[TD([[makeQuery(id+"F16.imprint","IMPRINT",EDGE,{"derivedFrom":sQuery(id+"F16.wireOp",EDGE,"E315.MirrorCS")}),1.0]])]});
            extrude(context, id + "F19", {"entities" : qUnion([Q0, Q1, Q2]), "operationType" : NewBodyOperationType.ADD, "depth" : 10 * mm, "offsetDistance" : 25 * mm});
        }
        {
            var Q0;
            Q0=makeQuery(id+"F1.opExtrude","SWEPT_FACE",FACE,{"disambiguationData":[OSD([sQuery(id+"F0.wireOp",EDGE,"E1.left"),sQuery(id+"F0.wireOp",EDGE,"E4.MirrorCS"),sQuery(id+"F0.wireOp",EDGE,"E12"),sQuery(id+"F0.wireOp",EDGE,"E13")])]});
            var sketch = newSketch(context, id + "F20", { "sketchPlane" : qUnion([Q0])});
            skLineSegment(sketch, "E384", {"start": v(-67, -30) * mm, "end": v(-67, 0) * mm});
            skFitSpline(sketch, "E385", {"points": [v(-67, -30) * mm, v(-71.65, -23.82) * mm, v(-73.03, -16.23) * mm, v(-74.55, -9.18) * mm, v(-80, -1.17) * mm], "startDerivative": vector(-22.4, 23.58) * mm, "endDerivative": vector(-23.42, 29.28) * mm});
            skLineSegment(sketch, "E386", {"start": v(-67, -30) * mm, "end": v(-80, -30) * mm});
            skLineSegment(sketch, "E387", {"start": v(-80, -30) * mm, "end": v(-80, -1.17) * mm});
            skLineSegment(sketch, "E388.MirrorCS", {"start": v(67, -30) * mm, "end": v(80, -30) * mm});
            skFitSpline(sketch, "E389.MirrorCS", {"points": [v(67, -30) * mm, v(71.65, -23.82) * mm, v(73.03, -16.23) * mm, v(74.55, -9.18) * mm, v(80, -1.17) * mm], "startDerivative": vector(22.4, 23.58) * mm, "endDerivative": vector(23.42, 29.28) * mm});
            skLineSegment(sketch, "E390.MirrorCS", {"start": v(80, -30) * mm, "end": v(80, -1.17) * mm});
            skLineSegment(sketch, "E391.MirrorCS", {"start": v(67, -30) * mm, "end": v(67, 0) * mm});
            skSolve(sketch);
        }
        {
            var Q0;
            Q0=makeQuery(id+"F20.imprint","IMPRINT",FACE,{"disambiguationData":[TD([[makeQuery(id+"F20.imprint","IMPRINT",EDGE,{"derivedFrom":sQuery(id+"F20.wireOp",EDGE,"E390.MirrorCS")}),1.0]])]});
            var Q1;
            Q1=makeQuery(id+"F20.imprint","IMPRINT",FACE,{"disambiguationData":[TD([[makeQuery(id+"F20.imprint","IMPRINT",EDGE,{"derivedFrom":sQuery(id+"F20.wireOp",EDGE,"E385")}),1.0]])]});
            extrude(context, id + "F21", {"entities" : qUnion([Q0, Q1]), "operationType" : NewBodyOperationType.REMOVE, "oppositeDirection" : true, "depth" : 210 * mm, "offsetDistance" : 25 * mm});
        }
        {
            var Q0;
            Q0=qCreatedBy(makeId("Front.planeOp"),FACE);
            var sketch = newSketch(context, id + "F22", { "sketchPlane" : qUnion([Q0])});
            skLineSegment(sketch, "E392", {"start": v(84.29, -30) * mm, "end": v(84.29, 0) * mm});
            skLineSegment(sketch, "E393.MirrorCS", {"start": v(79.59, -30) * mm, "end": v(92.59, -30) * mm});
            skLineSegment(sketch, "E394.MirrorCS", {"start": v(92.59, -30) * mm, "end": v(92.59, -1.17) * mm});
            skFitSpline(sketch, "E395.MirrorCS", {"points": [v(84.59, -30) * mm, v(89.24, -23.83) * mm, v(90.62, -16.23) * mm, v(92.14, -9.18) * mm, v(97.59, -1.17) * mm], "startDerivative": vector(22.4, 23.58) * mm, "endDerivative": vector(23.42, 29.28) * mm});
            skLineSegment(sketch, "E396.MirrorCS", {"start": v(84.59, -30) * mm, "end": v(97.59, -30) * mm});
            skLineSegment(sketch, "E397.MirrorCS", {"start": v(97.59, -30) * mm, "end": v(97.59, -1.17) * mm});
            skSolve(sketch);
        }
        {
            var Q0;
            Q0=qSketchRegion(id+"F22",true);
            extrude(context, id + "F23", {"entities" : qUnion([Q0]), "operationType" : NewBodyOperationType.REMOVE, "oppositeDirection" : true, "depth" : 90 * mm, "offsetDistance" : 25 * mm, "hasSecondDirection" : true, "secondDirectionOppositeDirection" : false, "secondDirectionDepth" : 90 * mm});
        }
        {
            var Q0;
            Q0=makeQuery(id+"F7.opExtrude","SWEPT_FACE",FACE,{"disambiguationData":[OSD([sQuery(id+"F0.wireOp",EDGE,"E22"),sQuery(id+"F0.wireOp",EDGE,"E23")])]});
            var sketch = newSketch(context, id + "F24", { "sketchPlane" : qUnion([Q0])});
            skLineSegment(sketch, "E398", {"start": v(-67.32, -30) * mm, "end": v(-67.32, 0) * mm});
            skFitSpline(sketch, "E399", {"points": [v(-67.32, -30) * mm, v(-71.8, -23.82) * mm, v(-73.17, -16.23) * mm, v(-74.7, -9.18) * mm, v(-80.32, -1.17) * mm], "startDerivative": vector(-22.4, 23.58) * mm, "endDerivative": vector(-23.42, 29.28) * mm});
            skLineSegment(sketch, "E400", {"start": v(-67.32, -30) * mm, "end": v(-80.32, -30) * mm});
            skLineSegment(sketch, "E401", {"start": v(-80.32, -30) * mm, "end": v(-80.32, -1.17) * mm});
            skLineSegment(sketch, "E402.MirrorCS", {"start": v(67.06, -30) * mm, "end": v(67.06, 0) * mm});
            skLineSegment(sketch, "E403.MirrorCS", {"start": v(67.06, -30) * mm, "end": v(80.06, -30) * mm});
            skFitSpline(sketch, "E404.MirrorCS", {"points": [v(67.06, -30) * mm, v(71.7, -23.82) * mm, v(73.09, -16.23) * mm, v(74.6, -9.18) * mm, v(80.06, -1.17) * mm], "startDerivative": vector(22.4, 23.58) * mm, "endDerivative": vector(23.42, 29.28) * mm});
            skLineSegment(sketch, "E405", {"start": v(80.06, -30) * mm, "end": v(80.06, -1.17) * mm});
            skSolve(sketch);
        }
        {
            var Q0;
            {var subQ3=sQuery(id+"F24.wireOp",EDGE,"E405");Q0=makeQuery(id+"F24.imprint","IMPRINT",FACE,{"disambiguationData":[TD([[makeQuery(id+"F24.imprint","IMPRINT",EDGE,{"derivedFrom":subQ3}),1.0]])]});}
            var Q1;
            {var subQ0=sQuery(id+"F24.wireOp",EDGE,"E403.MirrorCS");var subQ1=sQuery(id+"F0.wireOp",EDGE,"E23");var subQ2=makeQuery(id+"F7.opExtrude","SWEPT_EDGE",EDGE,{"disambiguationData":[OSD([subQ1,sQuery(id+"F0.wireOp",EDGE,"E41")])]});var subQ3=makeQuery(id+"F24.imprint","INTERSECT",VERTEX,{"derivedFrom":[subQ2,subQ0]});Q1=makeQuery(id+"F24.imprint","IMPRINT",FACE,{"disambiguationData":[TD([[makeQuery(id+"F24.imprint","IMPRINT",EDGE,{"disambiguationData":[TD([[subQ3,-1.0]])],"derivedFrom":subQ2}),1.0]])]});}
            var Q2;
            Q2=makeQuery(id+"F24.imprint","IMPRINT",FACE,{"disambiguationData":[TD([[makeQuery(id+"F24.imprint","IMPRINT",EDGE,{"derivedFrom":sQuery(id+"F24.wireOp",EDGE,"E399")}),1.0]])]});
            extrude(context, id + "F25", {"entities" : qUnion([Q0, Q1, Q2]), "operationType" : NewBodyOperationType.REMOVE, "oppositeDirection" : true, "depth" : 40 * mm, "offsetDistance" : 25 * mm});
        }
        {
            var Q0;
            Q0=makeQuery(id+"F7.opExtrude","CAP_EDGE",EDGE,{"disambiguationData":[OSD([sQuery(id+"F0.wireOp",EDGE,"E158")])],"isStart":false});
            fillet(context, id + "F26", {"entities" : qUnion([Q0]), "radius" : 5 * mm, "tangentPropagation" : true, "allowEdgeOverflow" : false});
        }
        {
            var Q0;
            Q0 = qSketchRegion(id + "F0", true);
            var Q1;
            {var subQ8=sQuery(id+"F0.wireOp",EDGE,"5df04954-8eb5-4515-9e13-43a69edbc3d81.MirrorCS");Q1=makeQuery(id+"F0.imprint","IMPRINT",FACE,{"disambiguationData":[TD([[makeQuery(id+"F0.imprint","IMPRINT",EDGE,{"derivedFrom":subQ8}),-1.0]])]});}
            var Q2;
            {var subQ0=sQuery(id+"F0.wireOp",EDGE,"5df04954-8eb5-4515-9e13-43a69edbc3d81.MirrorCS");Q2=makeQuery(id+"F0.imprint","IMPRINT",FACE,{"disambiguationData":[TD([[makeQuery(id+"F0.imprint","IMPRINT",EDGE,{"derivedFrom":subQ0}),1.0]])]});}
            var Q3;
            {var subQ0=sQuery(id+"F0.wireOp",EDGE,"5df04954-8eb5-4515-9e13-43a69edbc3d810.MirrorCS");Q3=makeQuery(id+"F0.imprint","IMPRINT",FACE,{"disambiguationData":[TD([[makeQuery(id+"F0.imprint","IMPRINT",EDGE,{"derivedFrom":subQ0}),-1.0]])]});}
            var Q4;
            {var subQ0=sQuery(id+"F0.wireOp",EDGE,"5df04954-8eb5-4515-9e13-43a69edbc3d86.MirrorCS");Q4=makeQuery(id+"F0.imprint","IMPRINT",FACE,{"disambiguationData":[TD([[makeQuery(id+"F0.imprint","IMPRINT",EDGE,{"derivedFrom":subQ0}),-1.0]])]});}
            var Q5;
            {var subQ0=sQuery(id+"F0.wireOp",EDGE,"5df04954-8eb5-4515-9e13-43a69edbc3d84.MirrorCS");Q5=makeQuery(id+"F0.imprint","IMPRINT",FACE,{"disambiguationData":[TD([[makeQuery(id+"F0.imprint","IMPRINT",EDGE,{"derivedFrom":subQ0}),-1.0]])]});}
            var Q6;
            Q6=makeQuery(id+"F0.imprint","IMPRINT",FACE,{"disambiguationData":[TD([[makeQuery(id+"F0.imprint","IMPRINT",EDGE,{"derivedFrom":sQuery(id+"F0.wireOp",EDGE,"5wepLe1d-8zNq-fh7S-O01Z-jGwKUINYCkkD")}),1.0]])]});
            var Q7;
            {var subQ0=sQuery(id+"F0.wireOp",EDGE,"5df04954-8eb5-4515-9e13-43a69edbc3d88.MirrorCS");var subQ1=sQuery(id+"F0.wireOp",EDGE,"5df04954-8eb5-4515-9e13-43a69edbc3d85.MirrorCS");var subQ2=makeQuery(id+"F0.imprint","INTERSECT",VERTEX,{"derivedFrom":[subQ1,subQ0]});Q7=makeQuery(id+"F0.imprint","IMPRINT",FACE,{"disambiguationData":[TD([[makeQuery(id+"F0.imprint","IMPRINT",EDGE,{"disambiguationData":[TD([[subQ2,1.0]])],"derivedFrom":subQ1}),-1.0]])]});}
            var Q8;
            {var subQ0=sQuery(id+"F0.wireOp",EDGE,"5df04954-8eb5-4515-9e13-43a69edbc3d812.MirrorCS");var subQ1=sQuery(id+"F0.wireOp",EDGE,"5df04954-8eb5-4515-9e13-43a69edbc3d82.MirrorCS");var subQ2=makeQuery(id+"F0.imprint","INTERSECT",VERTEX,{"derivedFrom":[subQ1,subQ0]});Q8=makeQuery(id+"F0.imprint","IMPRINT",FACE,{"disambiguationData":[TD([[makeQuery(id+"F0.imprint","IMPRINT",EDGE,{"disambiguationData":[TD([[subQ2,-1.0]])],"derivedFrom":subQ1}),1.0]])]});}
            var Q9;
            {var subQ0=sQuery(id+"F0.wireOp",EDGE,"H7Zu6mcE-TzpD-Prs2-afAv-bb7UNrpKUnZ3");var subQ1=sQuery(id+"F0.wireOp",EDGE,"62e97f5a-d78d-431a-af55-523a3b282b310.MirrorCS");var subQ2=makeQuery(id+"F0.imprint","INTERSECT",VERTEX,{"disambiguationData":[OD(0.0)],"derivedFrom":[subQ1,subQ0]});Q9=makeQuery(id+"F0.imprint","IMPRINT",FACE,{"disambiguationData":[TD([[makeQuery(id+"F0.imprint","IMPRINT",EDGE,{"disambiguationData":[TD([[subQ2,-1.0]])],"derivedFrom":subQ1}),-1.0]])]});}
            var Q10;
            {var subQ0=sQuery(id+"F0.wireOp",EDGE,"2953cc8a-75ce-4042-964e-4aa7a04384ec0.MirrorCS");var subQ1=sQuery(id+"F0.wireOp",EDGE,"62e97f5a-d78d-431a-af55-523a3b282b310.MirrorCS");var subQ2=makeQuery(id+"F0.imprint","INTERSECT",VERTEX,{"derivedFrom":[subQ1,subQ0]});Q10=makeQuery(id+"F0.imprint","IMPRINT",FACE,{"disambiguationData":[TD([[makeQuery(id+"F0.imprint","IMPRINT",EDGE,{"disambiguationData":[TD([[subQ2,-1.0]])],"derivedFrom":subQ1}),1.0]])]});}
            var Q11;
            {var subQ0=sQuery(id+"F0.wireOp",EDGE,"H7Zu6mcE-TzpD-Prs2-afAv-bb7UNrpKUnZ3");var subQ1=sQuery(id+"F0.wireOp",EDGE,"f532204f-58c9-45fd-867f-38ba44cf0707");var subQ2=makeQuery(id+"F0.imprint","INTERSECT",VERTEX,{"disambiguationData":[OD(0.0)],"derivedFrom":[subQ1,subQ0]});Q11=makeQuery(id+"F0.imprint","IMPRINT",FACE,{"disambiguationData":[TD([[makeQuery(id+"F0.imprint","IMPRINT",EDGE,{"disambiguationData":[TD([[subQ2,-1.0]])],"derivedFrom":subQ1}),1.0]])]});}
            var Q12;
            {var subQ0=sQuery(id+"F0.wireOp",EDGE,"b732a203-f060-4852-94d0-d5c29e6ce8c8");var subQ1=sQuery(id+"F0.wireOp",EDGE,"f532204f-58c9-45fd-867f-38ba44cf0707");var subQ2=makeQuery(id+"F0.imprint","INTERSECT",VERTEX,{"derivedFrom":[subQ1,subQ0]});Q12=makeQuery(id+"F0.imprint","IMPRINT",FACE,{"disambiguationData":[TD([[makeQuery(id+"F0.imprint","IMPRINT",EDGE,{"disambiguationData":[TD([[subQ2,-1.0]])],"derivedFrom":subQ1}),-1.0]])]});}
            var Q13;
            {var subQ19=sQuery(id+"F0.wireOp",EDGE,"1e7b46df-daae-406a-85df-c87a7ed3f0fb");Q13=makeQuery(id+"F0.imprint","IMPRINT",FACE,{"disambiguationData":[TD([[makeQuery(id+"F0.imprint","IMPRINT",EDGE,{"derivedFrom":subQ19}),-1.0]])]});}
            var Q14;
            Q14=makeQuery(id+"F0.imprint","IMPRINT",FACE,{"disambiguationData":[TD([[makeQuery(id+"F0.imprint","IMPRINT",EDGE,{"derivedFrom":sQuery(id+"F0.wireOp",EDGE,"0GYmCeUH-uDPA-4tkL-0XiE-MzLGmWvWNgLI")}),1.0]])]});
            var Q15;
            {var subQ0=sQuery(id+"F0.wireOp",EDGE,"7baa0f8b-bd87-4a79-816f-f555f1973061");Q15=makeQuery(id+"F0.imprint","IMPRINT",FACE,{"disambiguationData":[TD([[makeQuery(id+"F0.imprint","IMPRINT",EDGE,{"derivedFrom":subQ0}),-1.0]])]});}
            var Q16;
            {var subQ0=sQuery(id+"F0.wireOp",EDGE,"a47eecba-8c5f-4a7c-900a-808ab747d87a.filletArc");Q16=makeQuery(id+"F0.imprint","IMPRINT",FACE,{"disambiguationData":[TD([[makeQuery(id+"F0.imprint","IMPRINT",EDGE,{"derivedFrom":subQ0}),1.0]])]});}
            var Q17;
            {var subQ0=sQuery(id+"F0.wireOp",EDGE,"1e5f49b8-77da-43ca-8d71-619981cc3dd5.filletArc");Q17=makeQuery(id+"F0.imprint","IMPRINT",FACE,{"disambiguationData":[TD([[makeQuery(id+"F0.imprint","IMPRINT",EDGE,{"derivedFrom":subQ0}),1.0]])]});}
            var Q18;
            {var subQ0=sQuery(id+"F0.wireOp",EDGE,"1e7b46df-daae-406a-85df-c87a7ed3f0fb");Q18=makeQuery(id+"F0.imprint","IMPRINT",FACE,{"disambiguationData":[TD([[makeQuery(id+"F0.imprint","IMPRINT",EDGE,{"derivedFrom":subQ0}),1.0]])]});}
            extrude(context, id + "F27", {"entities" : qUnion([Q0, Q1, Q2, Q3, Q4, Q5, Q6, Q7, Q8, Q9, Q10, Q11, Q12, Q13, Q14, Q15, Q16, Q17, Q18]), "oppositeDirection" : true, "depth" : 30 * mm, "offsetDistance" : 25 * mm});
        }
    });
